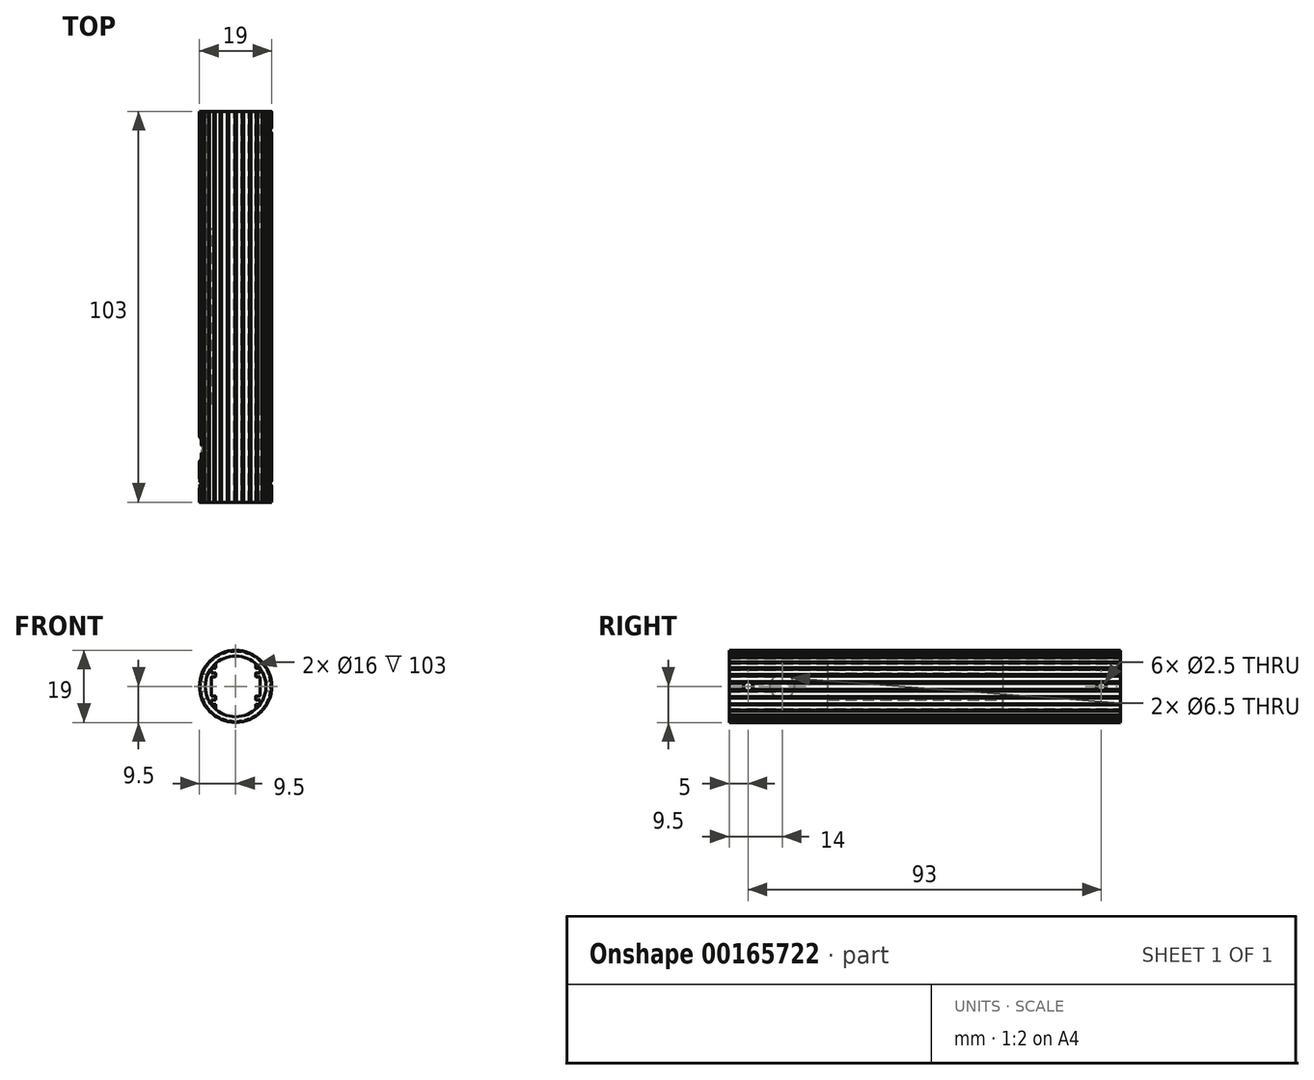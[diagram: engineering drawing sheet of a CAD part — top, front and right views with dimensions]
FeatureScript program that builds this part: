
annotation { "Feature Type Name" : "Feature", "Feature Type Description" : "" }
export const myFeature = defineFeature(function(context is Context, id is Id, definition is map)
    precondition{}
    {
        {
            assignVariable(context, id + "F0", {"name" : "Main_Length", "anyValue" : 103});
        }
        {
            assignVariable(context, id + "F1", {"name" : "Bore_Depth_F", "anyValue" : 26});
        }
        {
            assignVariable(context, id + "F2", {"name" : "Bore_Depth_R", "anyValue" : 31});
        }
        {
            var Q0;
            Q0=qCreatedBy(makeId("Front.planeOp"),FACE);
            var sketch = newSketch(context, id + "F3", { "sketchPlane" : qUnion([Q0])});
            skLineSegment(sketch, "E0", {"start": v(-5.25, -3.45) * mm, "end": v(-5.25, -2.65) * mm});
            skLineSegment(sketch, "E1", {"start": v(9.2, 1.38) * mm, "end": v(9.42, 1.2) * mm});
            skArc(sketch, "E2", {"start": v(-5.35, -2.55) * mm, "mid": v(-5.28, -2.58) * mm, "end": v(-5.25, -2.65) * mm});
            skArc(sketch, "E3", {"start": v(6.3, 4.75) * mm, "mid": v(6.37, 4.72) * mm, "end": v(6.4, 4.65) * mm});
            skArc(sketch, "E4", {"start": v(-5.25, -6.04) * mm, "mid": v(0, -8) * mm, "end": v(5.25, -6.04) * mm});
            skLineSegment(sketch, "E5", {"start": v(1.53, 9.17) * mm, "end": v(1.78, 9.33) * mm});
            skLineSegment(sketch, "E6", {"start": v(-7.18, -5.91) * mm, "end": v(-7.2, -6.2) * mm});
            skArc(sketch, "E7", {"start": v(-8.33, -4.58) * mm, "mid": v(-8.23, -4.75) * mm, "end": v(-8.13, -4.92) * mm});
            skLineSegment(sketch, "E8", {"start": v(5.13, 7.76) * mm, "end": v(5.42, 7.8) * mm});
            skLineSegment(sketch, "E9", {"start": v(6.4, -2.45) * mm, "end": v(6.4, 0) * mm});
            skLineSegment(sketch, "E10", {"start": v(-2.33, -9) * mm, "end": v(-2.17, -9.25) * mm});
            skArc(sketch, "E11", {"start": v(8.97, -3.13) * mm, "mid": v(9.04, -2.94) * mm, "end": v(9.1, -2.74) * mm});
            skArc(sketch, "E12", {"start": v(-4.05, -8.6) * mm, "mid": v(-3.86, -8.68) * mm, "end": v(-3.68, -8.76) * mm});
            skArc(sketch, "E13", {"start": v(4.05, 8.6) * mm, "mid": v(3.86, 8.68) * mm, "end": v(3.68, 8.76) * mm});
            skLineSegment(sketch, "E14", {"start": v(6.63, 6.52) * mm, "end": v(6.92, 6.5) * mm});
            skArc(sketch, "E15", {"start": v(-6.4, 3.65) * mm, "mid": v(-6.37, 3.58) * mm, "end": v(-6.3, 3.55) * mm});
            skArc(sketch, "E16", {"start": v(5.74, 7.57) * mm, "mid": v(5.58, 7.69) * mm, "end": v(5.42, 7.8) * mm});
            skLineSegment(sketch, "E17", {"start": v(-9.2, 1.38) * mm, "end": v(-9.42, 1.2) * mm});
            skArc(sketch, "E18", {"start": v(1.78, -9.33) * mm, "mid": v(1.98, -9.3) * mm, "end": v(2.17, -9.25) * mm});
            skLineSegment(sketch, "E19", {"start": v(-5.8, 7.28) * mm, "end": v(-5.74, 7.57) * mm});
            skArc(sketch, "E20", {"start": v(-2.17, -9.25) * mm, "mid": v(-1.98, -9.3) * mm, "end": v(-1.78, -9.33) * mm});
            skLineSegment(sketch, "E21", {"start": v(7.84, 5) * mm, "end": v(8.13, 4.92) * mm});
            skLineSegment(sketch, "E22", {"start": v(2.33, 9) * mm, "end": v(2.17, 9.25) * mm});
            skArc(sketch, "E23", {"start": v(5.25, -3.45) * mm, "mid": v(5.28, -3.52) * mm, "end": v(5.35, -3.55) * mm});
            skLineSegment(sketch, "E24", {"start": v(5.8, -7.28) * mm, "end": v(5.74, -7.57) * mm});
            skArc(sketch, "E25", {"start": v(5.35, 2.55) * mm, "mid": v(5.28, 2.58) * mm, "end": v(5.25, 2.65) * mm});
            skArc(sketch, "E26", {"start": v(4.15, -8.32) * mm, "mid": v(4.65, -8.05) * mm, "end": v(5.13, -7.76) * mm});
            skArc(sketch, "E27", {"start": v(-5.35, 4.75) * mm, "mid": v(-5.28, 4.78) * mm, "end": v(-5.25, 4.85) * mm});
            skArc(sketch, "E28", {"start": v(-8.13, 4.92) * mm, "mid": v(-8.23, 4.75) * mm, "end": v(-8.33, 4.58) * mm});
            skLineSegment(sketch, "E29", {"start": v(7.84, -5) * mm, "end": v(8.13, -4.92) * mm});
            skArc(sketch, "E30", {"start": v(8.33, 4.58) * mm, "mid": v(8.23, 4.75) * mm, "end": v(8.13, 4.92) * mm});
            skLineSegment(sketch, "E31", {"start": v(-6.3, 3.55) * mm, "end": v(-5.35, 3.55) * mm});
            skLineSegment(sketch, "E32", {"start": v(-5.25, 3.45) * mm, "end": v(-5.25, 2.65) * mm});
            skArc(sketch, "E33", {"start": v(9.1, 2.74) * mm, "mid": v(9.04, 2.94) * mm, "end": v(8.97, 3.13) * mm});
            skLineSegment(sketch, "E34", {"start": v(6.3, 3.55) * mm, "end": v(5.35, 3.55) * mm});
            skLineSegment(sketch, "E35", {"start": v(4.15, -8.32) * mm, "end": v(4.05, -8.6) * mm});
            skLineSegment(sketch, "E36", {"start": v(5.25, 6.04) * mm, "end": v(5.25, 4.85) * mm});
            skArc(sketch, "E37", {"start": v(8.71, 3.26) * mm, "mid": v(8.5, 3.78) * mm, "end": v(8.25, 4.3) * mm});
            skArc(sketch, "E38", {"start": v(0.4, -9.3) * mm, "mid": v(0.97, -9.25) * mm, "end": v(1.53, -9.17) * mm});
            skArc(sketch, "E39", {"start": v(9.47, 0.8) * mm, "mid": v(9.45, 1) * mm, "end": v(9.42, 1.2) * mm});
            skArc(sketch, "E40", {"start": v(-4.15, 8.32) * mm, "mid": v(-4.65, 8.05) * mm, "end": v(-5.13, 7.76) * mm});
            skLineSegment(sketch, "E41", {"start": v(-0.4, 9.3) * mm, "end": v(-0.2, 9.5) * mm});
            skLineSegment(sketch, "E42", {"start": v(8.25, 4.3) * mm, "end": v(8.33, 4.58) * mm});
            skLineSegment(sketch, "E43", {"start": v(2.33, -9) * mm, "end": v(2.17, -9.25) * mm});
            skArc(sketch, "E44", {"start": v(-0.4, 9.3) * mm, "mid": v(-0.97, 9.25) * mm, "end": v(-1.53, 9.17) * mm});
            skLineSegment(sketch, "E45", {"start": v(-5.13, 7.76) * mm, "end": v(-5.42, 7.8) * mm});
            skLineSegment(sketch, "E46", {"start": v(-2.33, 9) * mm, "end": v(-2.17, 9.25) * mm});
            skLineSegment(sketch, "E47", {"start": v(6.63, -6.52) * mm, "end": v(6.92, -6.5) * mm});
            skArc(sketch, "E48", {"start": v(9.42, -1.2) * mm, "mid": v(9.45, -1) * mm, "end": v(9.47, -0.8) * mm});
            skArc(sketch, "E49", {"start": v(-3.68, 8.76) * mm, "mid": v(-3.86, 8.68) * mm, "end": v(-4.05, 8.6) * mm});
            skArc(sketch, "E50", {"start": v(9.2, 1.38) * mm, "mid": v(9.1, 1.93) * mm, "end": v(8.96, 2.48) * mm});
            skArc(sketch, "E51", {"start": v(5.35, 4.75) * mm, "mid": v(5.28, 4.78) * mm, "end": v(5.25, 4.85) * mm});
            skLineSegment(sketch, "E52", {"start": v(5.25, 3.45) * mm, "end": v(5.25, 2.65) * mm});
            skArc(sketch, "E53", {"start": v(-0.2, -9.5) * mm, "mid": v(0, -9.5) * mm, "end": v(0.2, -9.5) * mm});
            skArc(sketch, "E54", {"start": v(7.2, 6.2) * mm, "mid": v(7.06, 6.36) * mm, "end": v(6.92, 6.5) * mm});
            skLineSegment(sketch, "E55", {"start": v(3.4, 8.65) * mm, "end": v(3.68, 8.76) * mm});
            skArc(sketch, "E56", {"start": v(6.4, 3.65) * mm, "mid": v(6.37, 3.58) * mm, "end": v(6.3, 3.55) * mm});
            skLineSegment(sketch, "E57", {"start": v(-6.4, -2.45) * mm, "end": v(-6.4, 0) * mm});
            skArc(sketch, "E58", {"start": v(-2.33, 9) * mm, "mid": v(-2.87, 8.84) * mm, "end": v(-3.4, 8.65) * mm});
            skLineSegment(sketch, "E59", {"start": v(-1.53, 9.17) * mm, "end": v(-1.78, 9.33) * mm});
            skLineSegment(sketch, "E60", {"start": v(0.4, -9.3) * mm, "end": v(0.2, -9.5) * mm});
            skArc(sketch, "E61", {"start": v(-6.92, 6.5) * mm, "mid": v(-7.06, 6.36) * mm, "end": v(-7.2, 6.2) * mm});
            skArc(sketch, "E62", {"start": v(-8.25, 4.3) * mm, "mid": v(-8.5, 3.78) * mm, "end": v(-8.71, 3.26) * mm});
            skArc(sketch, "E63", {"start": v(6.3, -4.75) * mm, "mid": v(6.37, -4.72) * mm, "end": v(6.4, -4.65) * mm});
            skLineSegment(sketch, "E64", {"start": v(-6.4, 4.65) * mm, "end": v(-6.4, 3.65) * mm});
            skLineSegment(sketch, "E65", {"start": v(-6.4, 2.45) * mm, "end": v(-6.4, 0) * mm});
            skArc(sketch, "E66", {"start": v(8.25, -4.3) * mm, "mid": v(8.5, -3.78) * mm, "end": v(8.71, -3.26) * mm});
            skArc(sketch, "E67", {"start": v(-6.3, 2.55) * mm, "mid": v(-6.37, 2.52) * mm, "end": v(-6.4, 2.45) * mm});
            skLineSegment(sketch, "E68", {"start": v(-5.25, 6.04) * mm, "end": v(-5.25, 4.85) * mm});
            skLineSegment(sketch, "E69", {"start": v(-5.35, 4.75) * mm, "end": v(-6.3, 4.75) * mm});
            skLineSegment(sketch, "E70", {"start": v(-5.35, 2.55) * mm, "end": v(-6.3, 2.55) * mm});
            skArc(sketch, "E71", {"start": v(-5.25, 3.45) * mm, "mid": v(-5.28, 3.52) * mm, "end": v(-5.35, 3.55) * mm});
            skArc(sketch, "E72", {"start": v(-5.35, 2.55) * mm, "mid": v(-5.28, 2.58) * mm, "end": v(-5.25, 2.65) * mm});
            skArc(sketch, "E73", {"start": v(-6.3, 4.75) * mm, "mid": v(-6.37, 4.72) * mm, "end": v(-6.4, 4.65) * mm});
            skArc(sketch, "E74", {"start": v(6.3, 2.55) * mm, "mid": v(6.37, 2.52) * mm, "end": v(6.4, 2.45) * mm});
            skLineSegment(sketch, "E75", {"start": v(5.35, 2.55) * mm, "end": v(6.3, 2.55) * mm});
            skArc(sketch, "E76", {"start": v(5.25, 3.45) * mm, "mid": v(5.28, 3.52) * mm, "end": v(5.35, 3.55) * mm});
            skArc(sketch, "E77", {"start": v(0.2, 9.5) * mm, "mid": v(0, 9.5) * mm, "end": v(-0.2, 9.5) * mm});
            skLineSegment(sketch, "E78", {"start": v(5.35, 4.75) * mm, "end": v(6.3, 4.75) * mm});
            skLineSegment(sketch, "E79", {"start": v(6.4, 2.45) * mm, "end": v(6.4, 0) * mm});
            skLineSegment(sketch, "E80", {"start": v(6.4, 4.65) * mm, "end": v(6.4, 3.65) * mm});
            skArc(sketch, "E81", {"start": v(-5.35, -4.75) * mm, "mid": v(-5.28, -4.78) * mm, "end": v(-5.25, -4.85) * mm});
            skLineSegment(sketch, "E82", {"start": v(-6.3, -3.55) * mm, "end": v(-5.35, -3.55) * mm});
            skLineSegment(sketch, "E83", {"start": v(-5.35, -2.55) * mm, "end": v(-6.3, -2.55) * mm});
            skArc(sketch, "E84", {"start": v(-5.25, -3.45) * mm, "mid": v(-5.28, -3.52) * mm, "end": v(-5.35, -3.55) * mm});
            skArc(sketch, "E85", {"start": v(-6.3, -2.55) * mm, "mid": v(-6.37, -2.52) * mm, "end": v(-6.4, -2.45) * mm});
            skArc(sketch, "E86", {"start": v(-6.4, -3.65) * mm, "mid": v(-6.37, -3.58) * mm, "end": v(-6.3, -3.55) * mm});
            skArc(sketch, "E87", {"start": v(-6.3, -4.75) * mm, "mid": v(-6.37, -4.72) * mm, "end": v(-6.4, -4.65) * mm});
            skArc(sketch, "E88", {"start": v(5.35, -2.55) * mm, "mid": v(5.28, -2.58) * mm, "end": v(5.25, -2.65) * mm});
            skLineSegment(sketch, "E89", {"start": v(-3.4, 8.65) * mm, "end": v(-3.68, 8.76) * mm});
            skArc(sketch, "E90", {"start": v(6.3, -2.55) * mm, "mid": v(6.37, -2.52) * mm, "end": v(6.4, -2.45) * mm});
            skLineSegment(sketch, "E91", {"start": v(5.35, -2.55) * mm, "end": v(6.3, -2.55) * mm});
            skArc(sketch, "E92", {"start": v(6.4, -3.65) * mm, "mid": v(6.37, -3.58) * mm, "end": v(6.3, -3.55) * mm});
            skLineSegment(sketch, "E93", {"start": v(6.3, -3.55) * mm, "end": v(5.35, -3.55) * mm});
            skArc(sketch, "E94", {"start": v(5.35, -4.75) * mm, "mid": v(5.28, -4.78) * mm, "end": v(5.25, -4.85) * mm});
            skLineSegment(sketch, "E95", {"start": v(-5.25, -6.04) * mm, "end": v(-5.25, -4.85) * mm});
            skLineSegment(sketch, "E96", {"start": v(5.25, -3.45) * mm, "end": v(5.25, -2.65) * mm});
            skLineSegment(sketch, "E97", {"start": v(6.4, -4.65) * mm, "end": v(6.4, -3.65) * mm});
            skLineSegment(sketch, "E98", {"start": v(-5.35, -4.75) * mm, "end": v(-6.3, -4.75) * mm});
            skArc(sketch, "E99", {"start": v(-8.97, 3.13) * mm, "mid": v(-9.04, 2.94) * mm, "end": v(-9.1, 2.74) * mm});
            skLineSegment(sketch, "E100", {"start": v(-6.4, -4.65) * mm, "end": v(-6.4, -3.65) * mm});
            skLineSegment(sketch, "E101", {"start": v(5.35, -4.75) * mm, "end": v(6.3, -4.75) * mm});
            skLineSegment(sketch, "E102", {"start": v(-7.84, 5) * mm, "end": v(-8.13, 4.92) * mm});
            skLineSegment(sketch, "E103", {"start": v(5.25, -6.04) * mm, "end": v(5.25, -4.85) * mm});
            skArc(sketch, "E104", {"start": v(5.25, 6.04) * mm, "mid": v(0, 8) * mm, "end": v(-5.25, 6.04) * mm});
            skLineSegment(sketch, "E105", {"start": v(-0.4, -9.3) * mm, "end": v(-0.2, -9.5) * mm});
            skArc(sketch, "E106", {"start": v(2.33, -9) * mm, "mid": v(2.87, -8.84) * mm, "end": v(3.4, -8.65) * mm});
            skLineSegment(sketch, "E107", {"start": v(1.53, -9.17) * mm, "end": v(1.78, -9.33) * mm});
            skArc(sketch, "E108", {"start": v(3.68, -8.76) * mm, "mid": v(3.86, -8.68) * mm, "end": v(4.05, -8.6) * mm});
            skArc(sketch, "E109", {"start": v(-9.1, -2.74) * mm, "mid": v(-9.04, -2.94) * mm, "end": v(-8.97, -3.13) * mm});
            skLineSegment(sketch, "E110", {"start": v(3.4, -8.65) * mm, "end": v(3.68, -8.76) * mm});
            skArc(sketch, "E111", {"start": v(5.8, -7.28) * mm, "mid": v(6.22, -6.91) * mm, "end": v(6.63, -6.52) * mm});
            skArc(sketch, "E112", {"start": v(5.42, -7.8) * mm, "mid": v(5.58, -7.69) * mm, "end": v(5.74, -7.57) * mm});
            skLineSegment(sketch, "E113", {"start": v(5.13, -7.76) * mm, "end": v(5.42, -7.8) * mm});
            skLineSegment(sketch, "E114", {"start": v(-5.13, -7.76) * mm, "end": v(-5.42, -7.8) * mm});
            skLineSegment(sketch, "E115", {"start": v(7.18, -5.91) * mm, "end": v(7.2, -6.2) * mm});
            skLineSegment(sketch, "E116", {"start": v(-6.63, -6.52) * mm, "end": v(-6.92, -6.5) * mm});
            skArc(sketch, "E117", {"start": v(8.13, -4.92) * mm, "mid": v(8.23, -4.75) * mm, "end": v(8.33, -4.58) * mm});
            skArc(sketch, "E118", {"start": v(6.92, -6.5) * mm, "mid": v(7.06, -6.36) * mm, "end": v(7.2, -6.2) * mm});
            skArc(sketch, "E119", {"start": v(-5.74, -7.57) * mm, "mid": v(-5.58, -7.69) * mm, "end": v(-5.42, -7.8) * mm});
            skArc(sketch, "E120", {"start": v(8.96, -2.48) * mm, "mid": v(9.1, -1.93) * mm, "end": v(9.2, -1.38) * mm});
            skLineSegment(sketch, "E121", {"start": v(8.96, -2.48) * mm, "end": v(9.1, -2.74) * mm});
            skLineSegment(sketch, "E122", {"start": v(8.71, -3.26) * mm, "end": v(8.97, -3.13) * mm});
            skArc(sketch, "E123", {"start": v(9.28, -0.57) * mm, "mid": v(9.3, 0) * mm, "end": v(9.28, 0.57) * mm});
            skLineSegment(sketch, "E124", {"start": v(9.28, -0.57) * mm, "end": v(9.47, -0.8) * mm});
            skLineSegment(sketch, "E125", {"start": v(-1.53, -9.17) * mm, "end": v(-1.78, -9.33) * mm});
            skLineSegment(sketch, "E126", {"start": v(9.2, -1.38) * mm, "end": v(9.42, -1.2) * mm});
            skLineSegment(sketch, "E127", {"start": v(8.71, 3.26) * mm, "end": v(8.97, 3.13) * mm});
            skLineSegment(sketch, "E128", {"start": v(8.96, 2.48) * mm, "end": v(9.1, 2.74) * mm});
            skArc(sketch, "E129", {"start": v(7.84, 5) * mm, "mid": v(7.52, 5.47) * mm, "end": v(7.18, 5.91) * mm});
            skArc(sketch, "E130", {"start": v(6.63, 6.52) * mm, "mid": v(6.22, 6.91) * mm, "end": v(5.8, 7.28) * mm});
            skLineSegment(sketch, "E131", {"start": v(7.18, 5.91) * mm, "end": v(7.2, 6.2) * mm});
            skArc(sketch, "E132", {"start": v(5.13, 7.76) * mm, "mid": v(4.65, 8.05) * mm, "end": v(4.15, 8.32) * mm});
            skLineSegment(sketch, "E133", {"start": v(5.8, 7.28) * mm, "end": v(5.74, 7.57) * mm});
            skArc(sketch, "E134", {"start": v(3.4, 8.65) * mm, "mid": v(2.87, 8.84) * mm, "end": v(2.33, 9) * mm});
            skLineSegment(sketch, "E135", {"start": v(4.15, 8.32) * mm, "end": v(4.05, 8.6) * mm});
            skArc(sketch, "E136", {"start": v(1.53, 9.17) * mm, "mid": v(0.97, 9.25) * mm, "end": v(0.4, 9.3) * mm});
            skArc(sketch, "E137", {"start": v(2.17, 9.25) * mm, "mid": v(1.98, 9.3) * mm, "end": v(1.78, 9.33) * mm});
            skLineSegment(sketch, "E138", {"start": v(0.4, 9.3) * mm, "end": v(0.2, 9.5) * mm});
            skArc(sketch, "E139", {"start": v(-1.78, 9.33) * mm, "mid": v(-1.98, 9.3) * mm, "end": v(-2.17, 9.25) * mm});
            skLineSegment(sketch, "E140", {"start": v(-4.15, 8.32) * mm, "end": v(-4.05, 8.6) * mm});
            skArc(sketch, "E141", {"start": v(-5.8, 7.28) * mm, "mid": v(-6.22, 6.91) * mm, "end": v(-6.63, 6.52) * mm});
            skArc(sketch, "E142", {"start": v(-5.42, 7.8) * mm, "mid": v(-5.58, 7.69) * mm, "end": v(-5.74, 7.57) * mm});
            skLineSegment(sketch, "E143", {"start": v(-9.2, -1.38) * mm, "end": v(-9.42, -1.2) * mm});
            skLineSegment(sketch, "E144", {"start": v(-7.18, 5.91) * mm, "end": v(-7.2, 6.2) * mm});
            skLineSegment(sketch, "E145", {"start": v(-6.63, 6.52) * mm, "end": v(-6.92, 6.5) * mm});
            skArc(sketch, "E146", {"start": v(-8.96, 2.48) * mm, "mid": v(-9.1, 1.93) * mm, "end": v(-9.2, 1.38) * mm});
            skLineSegment(sketch, "E147", {"start": v(-8.96, 2.48) * mm, "end": v(-9.1, 2.74) * mm});
            skLineSegment(sketch, "E148", {"start": v(-8.71, 3.26) * mm, "end": v(-8.97, 3.13) * mm});
            skArc(sketch, "E149", {"start": v(-9.28, 0.57) * mm, "mid": v(-9.3, 0) * mm, "end": v(-9.28, -0.57) * mm});
            skArc(sketch, "E150", {"start": v(-9.42, 1.2) * mm, "mid": v(-9.45, 1) * mm, "end": v(-9.47, 0.8) * mm});
            skLineSegment(sketch, "E151", {"start": v(-9.28, 0.57) * mm, "end": v(-9.47, 0.8) * mm});
            skLineSegment(sketch, "E152", {"start": v(8.25, -4.3) * mm, "end": v(8.33, -4.58) * mm});
            skArc(sketch, "E153", {"start": v(-9.2, -1.38) * mm, "mid": v(-9.1, -1.93) * mm, "end": v(-8.96, -2.48) * mm});
            skArc(sketch, "E154", {"start": v(-9.47, -0.8) * mm, "mid": v(-9.45, -1) * mm, "end": v(-9.42, -1.2) * mm});
            skLineSegment(sketch, "E155", {"start": v(-9.28, -0.57) * mm, "end": v(-9.47, -0.8) * mm});
            skArc(sketch, "E156", {"start": v(-8.71, -3.26) * mm, "mid": v(-8.5, -3.78) * mm, "end": v(-8.25, -4.3) * mm});
            skLineSegment(sketch, "E157", {"start": v(-8.71, -3.26) * mm, "end": v(-8.97, -3.13) * mm});
            skLineSegment(sketch, "E158", {"start": v(-8.96, -2.48) * mm, "end": v(-9.1, -2.74) * mm});
            skArc(sketch, "E159", {"start": v(-7.84, -5) * mm, "mid": v(-7.52, -5.47) * mm, "end": v(-7.18, -5.91) * mm});
            skLineSegment(sketch, "E160", {"start": v(-7.84, -5) * mm, "end": v(-8.13, -4.92) * mm});
            skLineSegment(sketch, "E161", {"start": v(-8.25, -4.3) * mm, "end": v(-8.33, -4.58) * mm});
            skArc(sketch, "E162", {"start": v(-6.63, -6.52) * mm, "mid": v(-6.22, -6.91) * mm, "end": v(-5.8, -7.28) * mm});
            skLineSegment(sketch, "E163", {"start": v(9.28, 0.57) * mm, "end": v(9.47, 0.8) * mm});
            skArc(sketch, "E164", {"start": v(-7.2, -6.2) * mm, "mid": v(-7.06, -6.36) * mm, "end": v(-6.92, -6.5) * mm});
            skArc(sketch, "E165", {"start": v(7.18, -5.91) * mm, "mid": v(7.52, -5.47) * mm, "end": v(7.84, -5) * mm});
            skLineSegment(sketch, "E166", {"start": v(-5.8, -7.28) * mm, "end": v(-5.74, -7.57) * mm});
            skArc(sketch, "E167", {"start": v(-3.4, -8.65) * mm, "mid": v(-2.87, -8.84) * mm, "end": v(-2.33, -9) * mm});
            skLineSegment(sketch, "E168", {"start": v(-3.4, -8.65) * mm, "end": v(-3.68, -8.76) * mm});
            skLineSegment(sketch, "E169", {"start": v(-4.15, -8.32) * mm, "end": v(-4.05, -8.6) * mm});
            skArc(sketch, "E170", {"start": v(-1.53, -9.17) * mm, "mid": v(-0.97, -9.25) * mm, "end": v(-0.4, -9.3) * mm});
            skArc(sketch, "E171", {"start": v(-7.18, 5.91) * mm, "mid": v(-7.52, 5.47) * mm, "end": v(-7.84, 5) * mm});
            skLineSegment(sketch, "E172", {"start": v(-8.25, 4.3) * mm, "end": v(-8.33, 4.58) * mm});
            skArc(sketch, "E173", {"start": v(-5.13, -7.76) * mm, "mid": v(-4.65, -8.05) * mm, "end": v(-4.15, -8.32) * mm});
            skSolve(sketch);
        }
        {
            var Q0;
            Q0=makeQuery(id+"F3.imprint","IMPRINT",FACE,{"disambiguationData":[TD([[makeQuery(id+"F3.imprint","IMPRINT",EDGE,{"derivedFrom":sQuery(id+"F3.wireOp",EDGE,"E0")}),1.0]])]});
            extrude(context, id + "F4", {"entities" : qUnion([Q0]), "depth" : (getVariable(context, 'Main_Length') - getVariable(context, 'Bore_Depth_F') - getVariable(context, 'Bore_Depth_R')) * mm});
        }
        {
            var Q0;
            Q0=makeQuery(id+"F4.opExtrude","CAP_FACE",FACE,{"disambiguationData":[OSD([sQuery(id+"F3.wireOp",EDGE,"E0"),sQuery(id+"F3.wireOp",EDGE,"E1"),sQuery(id+"F3.wireOp",EDGE,"E2"),sQuery(id+"F3.wireOp",EDGE,"E3"),sQuery(id+"F3.wireOp",EDGE,"E4"),sQuery(id+"F3.wireOp",EDGE,"E5"),sQuery(id+"F3.wireOp",EDGE,"E6"),sQuery(id+"F3.wireOp",EDGE,"E7"),sQuery(id+"F3.wireOp",EDGE,"E8"),sQuery(id+"F3.wireOp",EDGE,"E9"),sQuery(id+"F3.wireOp",EDGE,"E10"),sQuery(id+"F3.wireOp",EDGE,"E11"),sQuery(id+"F3.wireOp",EDGE,"E12"),sQuery(id+"F3.wireOp",EDGE,"E13"),sQuery(id+"F3.wireOp",EDGE,"E14"),sQuery(id+"F3.wireOp",EDGE,"E15"),sQuery(id+"F3.wireOp",EDGE,"E16"),sQuery(id+"F3.wireOp",EDGE,"E17"),sQuery(id+"F3.wireOp",EDGE,"E18"),sQuery(id+"F3.wireOp",EDGE,"E19"),sQuery(id+"F3.wireOp",EDGE,"E20"),sQuery(id+"F3.wireOp",EDGE,"E21"),sQuery(id+"F3.wireOp",EDGE,"E22"),sQuery(id+"F3.wireOp",EDGE,"E23"),sQuery(id+"F3.wireOp",EDGE,"E24"),sQuery(id+"F3.wireOp",EDGE,"E25"),sQuery(id+"F3.wireOp",EDGE,"E26"),sQuery(id+"F3.wireOp",EDGE,"E27"),sQuery(id+"F3.wireOp",EDGE,"E28"),sQuery(id+"F3.wireOp",EDGE,"E29"),sQuery(id+"F3.wireOp",EDGE,"E30"),sQuery(id+"F3.wireOp",EDGE,"E31"),sQuery(id+"F3.wireOp",EDGE,"E32"),sQuery(id+"F3.wireOp",EDGE,"E33"),sQuery(id+"F3.wireOp",EDGE,"E34"),sQuery(id+"F3.wireOp",EDGE,"E35"),sQuery(id+"F3.wireOp",EDGE,"E36"),sQuery(id+"F3.wireOp",EDGE,"E37"),sQuery(id+"F3.wireOp",EDGE,"E38"),sQuery(id+"F3.wireOp",EDGE,"E39"),sQuery(id+"F3.wireOp",EDGE,"E40"),sQuery(id+"F3.wireOp",EDGE,"E41"),sQuery(id+"F3.wireOp",EDGE,"E42"),sQuery(id+"F3.wireOp",EDGE,"E43"),sQuery(id+"F3.wireOp",EDGE,"E44"),sQuery(id+"F3.wireOp",EDGE,"E45"),sQuery(id+"F3.wireOp",EDGE,"E46"),sQuery(id+"F3.wireOp",EDGE,"E47"),sQuery(id+"F3.wireOp",EDGE,"E48"),sQuery(id+"F3.wireOp",EDGE,"E49"),sQuery(id+"F3.wireOp",EDGE,"E50"),sQuery(id+"F3.wireOp",EDGE,"E51"),sQuery(id+"F3.wireOp",EDGE,"E52"),sQuery(id+"F3.wireOp",EDGE,"E53"),sQuery(id+"F3.wireOp",EDGE,"E54"),sQuery(id+"F3.wireOp",EDGE,"E55"),sQuery(id+"F3.wireOp",EDGE,"E56"),sQuery(id+"F3.wireOp",EDGE,"E57"),sQuery(id+"F3.wireOp",EDGE,"E58"),sQuery(id+"F3.wireOp",EDGE,"E59"),sQuery(id+"F3.wireOp",EDGE,"E60"),sQuery(id+"F3.wireOp",EDGE,"E61"),sQuery(id+"F3.wireOp",EDGE,"E62"),sQuery(id+"F3.wireOp",EDGE,"E63"),sQuery(id+"F3.wireOp",EDGE,"E64"),sQuery(id+"F3.wireOp",EDGE,"E65"),sQuery(id+"F3.wireOp",EDGE,"E66"),sQuery(id+"F3.wireOp",EDGE,"E67"),sQuery(id+"F3.wireOp",EDGE,"E68"),sQuery(id+"F3.wireOp",EDGE,"E69"),sQuery(id+"F3.wireOp",EDGE,"E70"),sQuery(id+"F3.wireOp",EDGE,"E71"),sQuery(id+"F3.wireOp",EDGE,"E72"),sQuery(id+"F3.wireOp",EDGE,"E73"),sQuery(id+"F3.wireOp",EDGE,"E74"),sQuery(id+"F3.wireOp",EDGE,"E75"),sQuery(id+"F3.wireOp",EDGE,"E76"),sQuery(id+"F3.wireOp",EDGE,"E77"),sQuery(id+"F3.wireOp",EDGE,"E78"),sQuery(id+"F3.wireOp",EDGE,"E79"),sQuery(id+"F3.wireOp",EDGE,"E80"),sQuery(id+"F3.wireOp",EDGE,"E81"),sQuery(id+"F3.wireOp",EDGE,"E82"),sQuery(id+"F3.wireOp",EDGE,"E83"),sQuery(id+"F3.wireOp",EDGE,"E84"),sQuery(id+"F3.wireOp",EDGE,"E85"),sQuery(id+"F3.wireOp",EDGE,"E86"),sQuery(id+"F3.wireOp",EDGE,"E87"),sQuery(id+"F3.wireOp",EDGE,"E88"),sQuery(id+"F3.wireOp",EDGE,"E89"),sQuery(id+"F3.wireOp",EDGE,"E90"),sQuery(id+"F3.wireOp",EDGE,"E91"),sQuery(id+"F3.wireOp",EDGE,"E92"),sQuery(id+"F3.wireOp",EDGE,"E93"),sQuery(id+"F3.wireOp",EDGE,"E94"),sQuery(id+"F3.wireOp",EDGE,"E95"),sQuery(id+"F3.wireOp",EDGE,"E96"),sQuery(id+"F3.wireOp",EDGE,"E97"),sQuery(id+"F3.wireOp",EDGE,"E98"),sQuery(id+"F3.wireOp",EDGE,"E99"),sQuery(id+"F3.wireOp",EDGE,"E100"),sQuery(id+"F3.wireOp",EDGE,"E101"),sQuery(id+"F3.wireOp",EDGE,"E102"),sQuery(id+"F3.wireOp",EDGE,"E103"),sQuery(id+"F3.wireOp",EDGE,"E104"),sQuery(id+"F3.wireOp",EDGE,"E105"),sQuery(id+"F3.wireOp",EDGE,"E106"),sQuery(id+"F3.wireOp",EDGE,"E107"),sQuery(id+"F3.wireOp",EDGE,"E108"),sQuery(id+"F3.wireOp",EDGE,"E109"),sQuery(id+"F3.wireOp",EDGE,"E110"),sQuery(id+"F3.wireOp",EDGE,"E111"),sQuery(id+"F3.wireOp",EDGE,"E112"),sQuery(id+"F3.wireOp",EDGE,"E113"),sQuery(id+"F3.wireOp",EDGE,"E114"),sQuery(id+"F3.wireOp",EDGE,"E115"),sQuery(id+"F3.wireOp",EDGE,"E116"),sQuery(id+"F3.wireOp",EDGE,"E117"),sQuery(id+"F3.wireOp",EDGE,"E118"),sQuery(id+"F3.wireOp",EDGE,"E119"),sQuery(id+"F3.wireOp",EDGE,"E120"),sQuery(id+"F3.wireOp",EDGE,"E121"),sQuery(id+"F3.wireOp",EDGE,"E122"),sQuery(id+"F3.wireOp",EDGE,"E123"),sQuery(id+"F3.wireOp",EDGE,"E124"),sQuery(id+"F3.wireOp",EDGE,"E125"),sQuery(id+"F3.wireOp",EDGE,"E126"),sQuery(id+"F3.wireOp",EDGE,"E127"),sQuery(id+"F3.wireOp",EDGE,"E128"),sQuery(id+"F3.wireOp",EDGE,"E129"),sQuery(id+"F3.wireOp",EDGE,"E130"),sQuery(id+"F3.wireOp",EDGE,"E131"),sQuery(id+"F3.wireOp",EDGE,"E132"),sQuery(id+"F3.wireOp",EDGE,"E133"),sQuery(id+"F3.wireOp",EDGE,"E134"),sQuery(id+"F3.wireOp",EDGE,"E135"),sQuery(id+"F3.wireOp",EDGE,"E136"),sQuery(id+"F3.wireOp",EDGE,"E137"),sQuery(id+"F3.wireOp",EDGE,"E138"),sQuery(id+"F3.wireOp",EDGE,"E139"),sQuery(id+"F3.wireOp",EDGE,"E140"),sQuery(id+"F3.wireOp",EDGE,"E141"),sQuery(id+"F3.wireOp",EDGE,"E142"),sQuery(id+"F3.wireOp",EDGE,"E143"),sQuery(id+"F3.wireOp",EDGE,"E144"),sQuery(id+"F3.wireOp",EDGE,"E145"),sQuery(id+"F3.wireOp",EDGE,"E146"),sQuery(id+"F3.wireOp",EDGE,"E147"),sQuery(id+"F3.wireOp",EDGE,"E148"),sQuery(id+"F3.wireOp",EDGE,"E149"),sQuery(id+"F3.wireOp",EDGE,"E150"),sQuery(id+"F3.wireOp",EDGE,"E151"),sQuery(id+"F3.wireOp",EDGE,"E152"),sQuery(id+"F3.wireOp",EDGE,"E153"),sQuery(id+"F3.wireOp",EDGE,"E154"),sQuery(id+"F3.wireOp",EDGE,"E155"),sQuery(id+"F3.wireOp",EDGE,"E156"),sQuery(id+"F3.wireOp",EDGE,"E157"),sQuery(id+"F3.wireOp",EDGE,"E158"),sQuery(id+"F3.wireOp",EDGE,"E159"),sQuery(id+"F3.wireOp",EDGE,"E160"),sQuery(id+"F3.wireOp",EDGE,"E161"),sQuery(id+"F3.wireOp",EDGE,"E162"),sQuery(id+"F3.wireOp",EDGE,"E163"),sQuery(id+"F3.wireOp",EDGE,"E164"),sQuery(id+"F3.wireOp",EDGE,"E165"),sQuery(id+"F3.wireOp",EDGE,"E166"),sQuery(id+"F3.wireOp",EDGE,"E167"),sQuery(id+"F3.wireOp",EDGE,"E168"),sQuery(id+"F3.wireOp",EDGE,"E169"),sQuery(id+"F3.wireOp",EDGE,"E170"),sQuery(id+"F3.wireOp",EDGE,"E171"),sQuery(id+"F3.wireOp",EDGE,"E172"),sQuery(id+"F3.wireOp",EDGE,"E173")])],"isStart":false});
            var sketch = newSketch(context, id + "F5", { "sketchPlane" : qUnion([Q0])});
            skCircle(sketch, "E174", {"center": v(0, 0) * mm, "radius": 8 * mm});
            skLineSegment(sketch, "E175.0.0", {"start": v(9.42, 1.2) * mm, "end": v(9.2, 1.38) * mm});
            skArc(sketch, "E175.0.1", {"start": v(9.2, 1.38) * mm, "mid": v(9.1, 1.93) * mm, "end": v(8.96, 2.48) * mm});
            skLineSegment(sketch, "E175.0.2", {"start": v(8.96, 2.48) * mm, "end": v(9.1, 2.74) * mm});
            skArc(sketch, "E175.0.3", {"start": v(9.1, 2.74) * mm, "mid": v(9.04, 2.94) * mm, "end": v(8.97, 3.13) * mm});
            skLineSegment(sketch, "E175.0.4", {"start": v(8.97, 3.13) * mm, "end": v(8.71, 3.26) * mm});
            skArc(sketch, "E175.0.5", {"start": v(8.71, 3.26) * mm, "mid": v(8.5, 3.78) * mm, "end": v(8.25, 4.3) * mm});
            skLineSegment(sketch, "E175.0.6", {"start": v(8.25, 4.3) * mm, "end": v(8.33, 4.58) * mm});
            skArc(sketch, "E175.0.7", {"start": v(8.33, 4.58) * mm, "mid": v(8.23, 4.75) * mm, "end": v(8.13, 4.92) * mm});
            skLineSegment(sketch, "E175.0.8", {"start": v(8.13, 4.92) * mm, "end": v(7.84, 5) * mm});
            skArc(sketch, "E175.0.9", {"start": v(7.84, 5) * mm, "mid": v(7.52, 5.47) * mm, "end": v(7.18, 5.91) * mm});
            skLineSegment(sketch, "E175.0.10", {"start": v(7.18, 5.91) * mm, "end": v(7.2, 6.2) * mm});
            skArc(sketch, "E175.0.11", {"start": v(7.2, 6.2) * mm, "mid": v(7.06, 6.36) * mm, "end": v(6.92, 6.5) * mm});
            skLineSegment(sketch, "E175.0.12", {"start": v(6.92, 6.5) * mm, "end": v(6.63, 6.52) * mm});
            skArc(sketch, "E175.0.13", {"start": v(6.63, 6.52) * mm, "mid": v(6.22, 6.91) * mm, "end": v(5.8, 7.28) * mm});
            skLineSegment(sketch, "E175.0.14", {"start": v(5.8, 7.28) * mm, "end": v(5.74, 7.57) * mm});
            skArc(sketch, "E175.0.15", {"start": v(5.74, 7.57) * mm, "mid": v(5.58, 7.69) * mm, "end": v(5.42, 7.8) * mm});
            skLineSegment(sketch, "E175.0.16", {"start": v(5.42, 7.8) * mm, "end": v(5.13, 7.76) * mm});
            skArc(sketch, "E175.0.17", {"start": v(5.13, 7.76) * mm, "mid": v(4.65, 8.05) * mm, "end": v(4.15, 8.32) * mm});
            skLineSegment(sketch, "E175.0.18", {"start": v(4.15, 8.32) * mm, "end": v(4.05, 8.6) * mm});
            skArc(sketch, "E175.0.19", {"start": v(4.05, 8.6) * mm, "mid": v(3.86, 8.68) * mm, "end": v(3.68, 8.76) * mm});
            skLineSegment(sketch, "E175.0.20", {"start": v(3.68, 8.76) * mm, "end": v(3.4, 8.65) * mm});
            skArc(sketch, "E175.0.21", {"start": v(3.4, 8.65) * mm, "mid": v(2.87, 8.84) * mm, "end": v(2.33, 9) * mm});
            skLineSegment(sketch, "E175.0.22", {"start": v(2.33, 9) * mm, "end": v(2.17, 9.25) * mm});
            skArc(sketch, "E175.0.23", {"start": v(2.17, 9.25) * mm, "mid": v(1.98, 9.3) * mm, "end": v(1.78, 9.33) * mm});
            skLineSegment(sketch, "E175.0.24", {"start": v(1.78, 9.33) * mm, "end": v(1.53, 9.17) * mm});
            skArc(sketch, "E175.0.25", {"start": v(1.53, 9.17) * mm, "mid": v(0.97, 9.25) * mm, "end": v(0.4, 9.3) * mm});
            skLineSegment(sketch, "E175.0.26", {"start": v(0.4, 9.3) * mm, "end": v(0.2, 9.5) * mm});
            skArc(sketch, "E175.0.27", {"start": v(0.2, 9.5) * mm, "mid": v(0, 9.5) * mm, "end": v(-0.2, 9.5) * mm});
            skLineSegment(sketch, "E175.0.28", {"start": v(-0.2, 9.5) * mm, "end": v(-0.4, 9.3) * mm});
            skArc(sketch, "E175.0.29", {"start": v(-0.4, 9.3) * mm, "mid": v(-0.97, 9.25) * mm, "end": v(-1.53, 9.17) * mm});
            skLineSegment(sketch, "E175.0.30", {"start": v(-1.53, 9.17) * mm, "end": v(-1.78, 9.33) * mm});
            skArc(sketch, "E175.0.31", {"start": v(-1.78, 9.33) * mm, "mid": v(-1.98, 9.3) * mm, "end": v(-2.17, 9.25) * mm});
            skLineSegment(sketch, "E175.0.32", {"start": v(-2.17, 9.25) * mm, "end": v(-2.33, 9) * mm});
            skArc(sketch, "E175.0.33", {"start": v(-2.33, 9) * mm, "mid": v(-2.87, 8.84) * mm, "end": v(-3.4, 8.65) * mm});
            skLineSegment(sketch, "E175.0.34", {"start": v(-3.4, 8.65) * mm, "end": v(-3.68, 8.76) * mm});
            skArc(sketch, "E175.0.35", {"start": v(-3.68, 8.76) * mm, "mid": v(-3.86, 8.68) * mm, "end": v(-4.05, 8.6) * mm});
            skLineSegment(sketch, "E175.0.36", {"start": v(-4.05, 8.6) * mm, "end": v(-4.15, 8.32) * mm});
            skArc(sketch, "E175.0.37", {"start": v(-4.15, 8.32) * mm, "mid": v(-4.65, 8.05) * mm, "end": v(-5.13, 7.76) * mm});
            skLineSegment(sketch, "E175.0.38", {"start": v(-5.13, 7.76) * mm, "end": v(-5.42, 7.8) * mm});
            skArc(sketch, "E175.0.39", {"start": v(-5.42, 7.8) * mm, "mid": v(-5.58, 7.69) * mm, "end": v(-5.74, 7.57) * mm});
            skLineSegment(sketch, "E175.0.40", {"start": v(-5.74, 7.57) * mm, "end": v(-5.8, 7.28) * mm});
            skArc(sketch, "E175.0.41", {"start": v(-5.8, 7.28) * mm, "mid": v(-6.22, 6.91) * mm, "end": v(-6.63, 6.52) * mm});
            skLineSegment(sketch, "E175.0.42", {"start": v(-6.63, 6.52) * mm, "end": v(-6.92, 6.5) * mm});
            skArc(sketch, "E175.0.43", {"start": v(-6.92, 6.5) * mm, "mid": v(-7.06, 6.36) * mm, "end": v(-7.2, 6.2) * mm});
            skLineSegment(sketch, "E175.0.44", {"start": v(-7.2, 6.2) * mm, "end": v(-7.18, 5.91) * mm});
            skArc(sketch, "E175.0.45", {"start": v(-7.18, 5.91) * mm, "mid": v(-7.52, 5.47) * mm, "end": v(-7.84, 5) * mm});
            skLineSegment(sketch, "E175.0.46", {"start": v(-7.84, 5) * mm, "end": v(-8.13, 4.92) * mm});
            skArc(sketch, "E175.0.47", {"start": v(-8.13, 4.92) * mm, "mid": v(-8.23, 4.75) * mm, "end": v(-8.33, 4.58) * mm});
            skLineSegment(sketch, "E175.0.48", {"start": v(-8.33, 4.58) * mm, "end": v(-8.25, 4.3) * mm});
            skArc(sketch, "E175.0.49", {"start": v(-8.25, 4.3) * mm, "mid": v(-8.5, 3.78) * mm, "end": v(-8.71, 3.26) * mm});
            skLineSegment(sketch, "E175.0.50", {"start": v(-8.71, 3.26) * mm, "end": v(-8.97, 3.13) * mm});
            skArc(sketch, "E175.0.51", {"start": v(-8.97, 3.13) * mm, "mid": v(-9.04, 2.94) * mm, "end": v(-9.1, 2.74) * mm});
            skLineSegment(sketch, "E175.0.52", {"start": v(-9.1, 2.74) * mm, "end": v(-8.96, 2.48) * mm});
            skArc(sketch, "E175.0.53", {"start": v(-8.96, 2.48) * mm, "mid": v(-9.1, 1.93) * mm, "end": v(-9.2, 1.38) * mm});
            skLineSegment(sketch, "E175.0.54", {"start": v(-9.2, 1.38) * mm, "end": v(-9.42, 1.2) * mm});
            skArc(sketch, "E175.0.55", {"start": v(-9.42, 1.2) * mm, "mid": v(-9.45, 1) * mm, "end": v(-9.47, 0.8) * mm});
            skLineSegment(sketch, "E175.0.56", {"start": v(-9.47, 0.8) * mm, "end": v(-9.28, 0.57) * mm});
            skArc(sketch, "E175.0.57", {"start": v(-9.28, 0.57) * mm, "mid": v(-9.3, 0) * mm, "end": v(-9.28, -0.57) * mm});
            skLineSegment(sketch, "E175.0.58", {"start": v(-9.28, -0.57) * mm, "end": v(-9.47, -0.8) * mm});
            skArc(sketch, "E175.0.59", {"start": v(-9.47, -0.8) * mm, "mid": v(-9.45, -1) * mm, "end": v(-9.42, -1.2) * mm});
            skLineSegment(sketch, "E175.0.60", {"start": v(-9.42, -1.2) * mm, "end": v(-9.2, -1.38) * mm});
            skArc(sketch, "E175.0.61", {"start": v(-9.2, -1.38) * mm, "mid": v(-9.1, -1.93) * mm, "end": v(-8.96, -2.48) * mm});
            skLineSegment(sketch, "E175.0.62", {"start": v(-8.96, -2.48) * mm, "end": v(-9.1, -2.74) * mm});
            skArc(sketch, "E175.0.63", {"start": v(-9.1, -2.74) * mm, "mid": v(-9.04, -2.94) * mm, "end": v(-8.97, -3.13) * mm});
            skLineSegment(sketch, "E175.0.64", {"start": v(-8.97, -3.13) * mm, "end": v(-8.71, -3.26) * mm});
            skArc(sketch, "E175.0.65", {"start": v(-8.71, -3.26) * mm, "mid": v(-8.5, -3.78) * mm, "end": v(-8.25, -4.3) * mm});
            skLineSegment(sketch, "E175.0.66", {"start": v(-8.25, -4.3) * mm, "end": v(-8.33, -4.58) * mm});
            skArc(sketch, "E175.0.67", {"start": v(-8.33, -4.58) * mm, "mid": v(-8.23, -4.75) * mm, "end": v(-8.13, -4.92) * mm});
            skLineSegment(sketch, "E175.0.68", {"start": v(-8.13, -4.92) * mm, "end": v(-7.84, -5) * mm});
            skArc(sketch, "E175.0.69", {"start": v(-7.84, -5) * mm, "mid": v(-7.52, -5.47) * mm, "end": v(-7.18, -5.91) * mm});
            skLineSegment(sketch, "E175.0.70", {"start": v(-7.18, -5.91) * mm, "end": v(-7.2, -6.2) * mm});
            skArc(sketch, "E175.0.71", {"start": v(-7.2, -6.2) * mm, "mid": v(-7.06, -6.36) * mm, "end": v(-6.92, -6.5) * mm});
            skLineSegment(sketch, "E175.0.72", {"start": v(-6.92, -6.5) * mm, "end": v(-6.63, -6.52) * mm});
            skArc(sketch, "E175.0.73", {"start": v(-6.63, -6.52) * mm, "mid": v(-6.22, -6.91) * mm, "end": v(-5.8, -7.28) * mm});
            skLineSegment(sketch, "E175.0.74", {"start": v(-5.8, -7.28) * mm, "end": v(-5.74, -7.57) * mm});
            skArc(sketch, "E175.0.75", {"start": v(-5.74, -7.57) * mm, "mid": v(-5.58, -7.69) * mm, "end": v(-5.42, -7.8) * mm});
            skLineSegment(sketch, "E175.0.76", {"start": v(-5.42, -7.8) * mm, "end": v(-5.13, -7.76) * mm});
            skArc(sketch, "E175.0.77", {"start": v(-5.13, -7.76) * mm, "mid": v(-4.65, -8.05) * mm, "end": v(-4.15, -8.32) * mm});
            skLineSegment(sketch, "E175.0.78", {"start": v(-4.15, -8.32) * mm, "end": v(-4.05, -8.6) * mm});
            skArc(sketch, "E175.0.79", {"start": v(-4.05, -8.6) * mm, "mid": v(-3.86, -8.68) * mm, "end": v(-3.68, -8.76) * mm});
            skLineSegment(sketch, "E175.0.80", {"start": v(-3.68, -8.76) * mm, "end": v(-3.4, -8.65) * mm});
            skArc(sketch, "E175.0.81", {"start": v(-3.4, -8.65) * mm, "mid": v(-2.87, -8.84) * mm, "end": v(-2.33, -9) * mm});
            skLineSegment(sketch, "E175.0.82", {"start": v(-2.33, -9) * mm, "end": v(-2.17, -9.25) * mm});
            skArc(sketch, "E175.0.83", {"start": v(-2.17, -9.25) * mm, "mid": v(-1.98, -9.3) * mm, "end": v(-1.78, -9.33) * mm});
            skLineSegment(sketch, "E175.0.84", {"start": v(-1.78, -9.33) * mm, "end": v(-1.53, -9.17) * mm});
            skArc(sketch, "E175.0.85", {"start": v(-1.53, -9.17) * mm, "mid": v(-0.97, -9.25) * mm, "end": v(-0.4, -9.3) * mm});
            skLineSegment(sketch, "E175.0.86", {"start": v(-0.4, -9.3) * mm, "end": v(-0.2, -9.5) * mm});
            skArc(sketch, "E175.0.87", {"start": v(-0.2, -9.5) * mm, "mid": v(0, -9.5) * mm, "end": v(0.2, -9.5) * mm});
            skLineSegment(sketch, "E175.0.88", {"start": v(0.2, -9.5) * mm, "end": v(0.4, -9.3) * mm});
            skArc(sketch, "E175.0.89", {"start": v(0.4, -9.3) * mm, "mid": v(0.97, -9.25) * mm, "end": v(1.53, -9.17) * mm});
            skLineSegment(sketch, "E175.0.90", {"start": v(1.53, -9.17) * mm, "end": v(1.78, -9.33) * mm});
            skArc(sketch, "E175.0.91", {"start": v(1.78, -9.33) * mm, "mid": v(1.98, -9.3) * mm, "end": v(2.17, -9.25) * mm});
            skLineSegment(sketch, "E175.0.92", {"start": v(2.17, -9.25) * mm, "end": v(2.33, -9) * mm});
            skArc(sketch, "E175.0.93", {"start": v(2.33, -9) * mm, "mid": v(2.87, -8.84) * mm, "end": v(3.4, -8.65) * mm});
            skLineSegment(sketch, "E175.0.94", {"start": v(3.4, -8.65) * mm, "end": v(3.68, -8.76) * mm});
            skArc(sketch, "E175.0.95", {"start": v(3.68, -8.76) * mm, "mid": v(3.86, -8.68) * mm, "end": v(4.05, -8.6) * mm});
            skLineSegment(sketch, "E175.0.96", {"start": v(4.05, -8.6) * mm, "end": v(4.15, -8.32) * mm});
            skArc(sketch, "E175.0.97", {"start": v(4.15, -8.32) * mm, "mid": v(4.65, -8.05) * mm, "end": v(5.13, -7.76) * mm});
            skLineSegment(sketch, "E175.0.98", {"start": v(5.13, -7.76) * mm, "end": v(5.42, -7.8) * mm});
            skArc(sketch, "E175.0.99", {"start": v(5.42, -7.8) * mm, "mid": v(5.58, -7.69) * mm, "end": v(5.74, -7.57) * mm});
            skLineSegment(sketch, "E175.0.100", {"start": v(5.74, -7.57) * mm, "end": v(5.8, -7.28) * mm});
            skArc(sketch, "E175.0.101", {"start": v(5.8, -7.28) * mm, "mid": v(6.22, -6.91) * mm, "end": v(6.63, -6.52) * mm});
            skLineSegment(sketch, "E175.0.102", {"start": v(6.63, -6.52) * mm, "end": v(6.92, -6.5) * mm});
            skArc(sketch, "E175.0.103", {"start": v(6.92, -6.5) * mm, "mid": v(7.06, -6.36) * mm, "end": v(7.2, -6.2) * mm});
            skLineSegment(sketch, "E175.0.104", {"start": v(7.2, -6.2) * mm, "end": v(7.18, -5.91) * mm});
            skArc(sketch, "E175.0.105", {"start": v(7.18, -5.91) * mm, "mid": v(7.52, -5.47) * mm, "end": v(7.84, -5) * mm});
            skLineSegment(sketch, "E175.0.106", {"start": v(7.84, -5) * mm, "end": v(8.13, -4.92) * mm});
            skArc(sketch, "E175.0.107", {"start": v(8.13, -4.92) * mm, "mid": v(8.23, -4.75) * mm, "end": v(8.33, -4.58) * mm});
            skLineSegment(sketch, "E175.0.108", {"start": v(8.33, -4.58) * mm, "end": v(8.25, -4.3) * mm});
            skArc(sketch, "E175.0.109", {"start": v(8.25, -4.3) * mm, "mid": v(8.5, -3.78) * mm, "end": v(8.71, -3.26) * mm});
            skLineSegment(sketch, "E175.0.110", {"start": v(8.71, -3.26) * mm, "end": v(8.97, -3.13) * mm});
            skArc(sketch, "E175.0.111", {"start": v(8.97, -3.13) * mm, "mid": v(9.04, -2.94) * mm, "end": v(9.1, -2.74) * mm});
            skLineSegment(sketch, "E175.0.112", {"start": v(9.1, -2.74) * mm, "end": v(8.96, -2.48) * mm});
            skArc(sketch, "E175.0.113", {"start": v(8.96, -2.48) * mm, "mid": v(9.1, -1.93) * mm, "end": v(9.2, -1.38) * mm});
            skLineSegment(sketch, "E175.0.114", {"start": v(9.2, -1.38) * mm, "end": v(9.42, -1.2) * mm});
            skArc(sketch, "E175.0.115", {"start": v(9.42, -1.2) * mm, "mid": v(9.45, -1) * mm, "end": v(9.47, -0.8) * mm});
            skLineSegment(sketch, "E175.0.116", {"start": v(9.47, -0.8) * mm, "end": v(9.28, -0.57) * mm});
            skArc(sketch, "E175.0.117", {"start": v(9.28, -0.57) * mm, "mid": v(9.3, 0) * mm, "end": v(9.28, 0.57) * mm});
            skLineSegment(sketch, "E175.0.118", {"start": v(9.28, 0.57) * mm, "end": v(9.47, 0.8) * mm});
            skArc(sketch, "E175.0.119", {"start": v(9.47, 0.8) * mm, "mid": v(9.45, 1) * mm, "end": v(9.42, 1.2) * mm});
            skSolve(sketch);
        }
        {
            var Q0;
            Q0=makeQuery(id+"F5.imprint","IMPRINT",FACE,{"disambiguationData":[TD([[makeQuery(id+"F5.imprint","IMPRINT",EDGE,{"derivedFrom":sQuery(id+"F5.wireOp",EDGE,"E175.0.0")}),-1.0]])]});
            extrude(context, id + "F6", {"entities" : qUnion([Q0]), "operationType" : NewBodyOperationType.ADD, "depth" : (getVariable(context, 'Bore_Depth_F')) * mm});
        }
        {
            var Q0;
            Q0=makeQuery(id+"F4.opExtrude","CAP_FACE",FACE,{"disambiguationData":[OSD([sQuery(id+"F3.wireOp",EDGE,"E0"),sQuery(id+"F3.wireOp",EDGE,"E1"),sQuery(id+"F3.wireOp",EDGE,"E2"),sQuery(id+"F3.wireOp",EDGE,"E3"),sQuery(id+"F3.wireOp",EDGE,"E4"),sQuery(id+"F3.wireOp",EDGE,"E5"),sQuery(id+"F3.wireOp",EDGE,"E6"),sQuery(id+"F3.wireOp",EDGE,"E7"),sQuery(id+"F3.wireOp",EDGE,"E8"),sQuery(id+"F3.wireOp",EDGE,"E9"),sQuery(id+"F3.wireOp",EDGE,"E10"),sQuery(id+"F3.wireOp",EDGE,"E11"),sQuery(id+"F3.wireOp",EDGE,"E12"),sQuery(id+"F3.wireOp",EDGE,"E13"),sQuery(id+"F3.wireOp",EDGE,"E14"),sQuery(id+"F3.wireOp",EDGE,"E15"),sQuery(id+"F3.wireOp",EDGE,"E16"),sQuery(id+"F3.wireOp",EDGE,"E17"),sQuery(id+"F3.wireOp",EDGE,"E18"),sQuery(id+"F3.wireOp",EDGE,"E19"),sQuery(id+"F3.wireOp",EDGE,"E20"),sQuery(id+"F3.wireOp",EDGE,"E21"),sQuery(id+"F3.wireOp",EDGE,"E22"),sQuery(id+"F3.wireOp",EDGE,"E23"),sQuery(id+"F3.wireOp",EDGE,"E24"),sQuery(id+"F3.wireOp",EDGE,"E25"),sQuery(id+"F3.wireOp",EDGE,"E26"),sQuery(id+"F3.wireOp",EDGE,"E27"),sQuery(id+"F3.wireOp",EDGE,"E28"),sQuery(id+"F3.wireOp",EDGE,"E29"),sQuery(id+"F3.wireOp",EDGE,"E30"),sQuery(id+"F3.wireOp",EDGE,"E31"),sQuery(id+"F3.wireOp",EDGE,"E32"),sQuery(id+"F3.wireOp",EDGE,"E33"),sQuery(id+"F3.wireOp",EDGE,"E34"),sQuery(id+"F3.wireOp",EDGE,"E35"),sQuery(id+"F3.wireOp",EDGE,"E36"),sQuery(id+"F3.wireOp",EDGE,"E37"),sQuery(id+"F3.wireOp",EDGE,"E38"),sQuery(id+"F3.wireOp",EDGE,"E39"),sQuery(id+"F3.wireOp",EDGE,"E40"),sQuery(id+"F3.wireOp",EDGE,"E41"),sQuery(id+"F3.wireOp",EDGE,"E42"),sQuery(id+"F3.wireOp",EDGE,"E43"),sQuery(id+"F3.wireOp",EDGE,"E44"),sQuery(id+"F3.wireOp",EDGE,"E45"),sQuery(id+"F3.wireOp",EDGE,"E46"),sQuery(id+"F3.wireOp",EDGE,"E47"),sQuery(id+"F3.wireOp",EDGE,"E48"),sQuery(id+"F3.wireOp",EDGE,"E49"),sQuery(id+"F3.wireOp",EDGE,"E50"),sQuery(id+"F3.wireOp",EDGE,"E51"),sQuery(id+"F3.wireOp",EDGE,"E52"),sQuery(id+"F3.wireOp",EDGE,"E53"),sQuery(id+"F3.wireOp",EDGE,"E54"),sQuery(id+"F3.wireOp",EDGE,"E55"),sQuery(id+"F3.wireOp",EDGE,"E56"),sQuery(id+"F3.wireOp",EDGE,"E57"),sQuery(id+"F3.wireOp",EDGE,"E58"),sQuery(id+"F3.wireOp",EDGE,"E59"),sQuery(id+"F3.wireOp",EDGE,"E60"),sQuery(id+"F3.wireOp",EDGE,"E61"),sQuery(id+"F3.wireOp",EDGE,"E62"),sQuery(id+"F3.wireOp",EDGE,"E63"),sQuery(id+"F3.wireOp",EDGE,"E64"),sQuery(id+"F3.wireOp",EDGE,"E65"),sQuery(id+"F3.wireOp",EDGE,"E66"),sQuery(id+"F3.wireOp",EDGE,"E67"),sQuery(id+"F3.wireOp",EDGE,"E68"),sQuery(id+"F3.wireOp",EDGE,"E69"),sQuery(id+"F3.wireOp",EDGE,"E70"),sQuery(id+"F3.wireOp",EDGE,"E71"),sQuery(id+"F3.wireOp",EDGE,"E72"),sQuery(id+"F3.wireOp",EDGE,"E73"),sQuery(id+"F3.wireOp",EDGE,"E74"),sQuery(id+"F3.wireOp",EDGE,"E75"),sQuery(id+"F3.wireOp",EDGE,"E76"),sQuery(id+"F3.wireOp",EDGE,"E77"),sQuery(id+"F3.wireOp",EDGE,"E78"),sQuery(id+"F3.wireOp",EDGE,"E79"),sQuery(id+"F3.wireOp",EDGE,"E80"),sQuery(id+"F3.wireOp",EDGE,"E81"),sQuery(id+"F3.wireOp",EDGE,"E82"),sQuery(id+"F3.wireOp",EDGE,"E83"),sQuery(id+"F3.wireOp",EDGE,"E84"),sQuery(id+"F3.wireOp",EDGE,"E85"),sQuery(id+"F3.wireOp",EDGE,"E86"),sQuery(id+"F3.wireOp",EDGE,"E87"),sQuery(id+"F3.wireOp",EDGE,"E88"),sQuery(id+"F3.wireOp",EDGE,"E89"),sQuery(id+"F3.wireOp",EDGE,"E90"),sQuery(id+"F3.wireOp",EDGE,"E91"),sQuery(id+"F3.wireOp",EDGE,"E92"),sQuery(id+"F3.wireOp",EDGE,"E93"),sQuery(id+"F3.wireOp",EDGE,"E94"),sQuery(id+"F3.wireOp",EDGE,"E95"),sQuery(id+"F3.wireOp",EDGE,"E96"),sQuery(id+"F3.wireOp",EDGE,"E97"),sQuery(id+"F3.wireOp",EDGE,"E98"),sQuery(id+"F3.wireOp",EDGE,"E99"),sQuery(id+"F3.wireOp",EDGE,"E100"),sQuery(id+"F3.wireOp",EDGE,"E101"),sQuery(id+"F3.wireOp",EDGE,"E102"),sQuery(id+"F3.wireOp",EDGE,"E103"),sQuery(id+"F3.wireOp",EDGE,"E104"),sQuery(id+"F3.wireOp",EDGE,"E105"),sQuery(id+"F3.wireOp",EDGE,"E106"),sQuery(id+"F3.wireOp",EDGE,"E107"),sQuery(id+"F3.wireOp",EDGE,"E108"),sQuery(id+"F3.wireOp",EDGE,"E109"),sQuery(id+"F3.wireOp",EDGE,"E110"),sQuery(id+"F3.wireOp",EDGE,"E111"),sQuery(id+"F3.wireOp",EDGE,"E112"),sQuery(id+"F3.wireOp",EDGE,"E113"),sQuery(id+"F3.wireOp",EDGE,"E114"),sQuery(id+"F3.wireOp",EDGE,"E115"),sQuery(id+"F3.wireOp",EDGE,"E116"),sQuery(id+"F3.wireOp",EDGE,"E117"),sQuery(id+"F3.wireOp",EDGE,"E118"),sQuery(id+"F3.wireOp",EDGE,"E119"),sQuery(id+"F3.wireOp",EDGE,"E120"),sQuery(id+"F3.wireOp",EDGE,"E121"),sQuery(id+"F3.wireOp",EDGE,"E122"),sQuery(id+"F3.wireOp",EDGE,"E123"),sQuery(id+"F3.wireOp",EDGE,"E124"),sQuery(id+"F3.wireOp",EDGE,"E125"),sQuery(id+"F3.wireOp",EDGE,"E126"),sQuery(id+"F3.wireOp",EDGE,"E127"),sQuery(id+"F3.wireOp",EDGE,"E128"),sQuery(id+"F3.wireOp",EDGE,"E129"),sQuery(id+"F3.wireOp",EDGE,"E130"),sQuery(id+"F3.wireOp",EDGE,"E131"),sQuery(id+"F3.wireOp",EDGE,"E132"),sQuery(id+"F3.wireOp",EDGE,"E133"),sQuery(id+"F3.wireOp",EDGE,"E134"),sQuery(id+"F3.wireOp",EDGE,"E135"),sQuery(id+"F3.wireOp",EDGE,"E136"),sQuery(id+"F3.wireOp",EDGE,"E137"),sQuery(id+"F3.wireOp",EDGE,"E138"),sQuery(id+"F3.wireOp",EDGE,"E139"),sQuery(id+"F3.wireOp",EDGE,"E140"),sQuery(id+"F3.wireOp",EDGE,"E141"),sQuery(id+"F3.wireOp",EDGE,"E142"),sQuery(id+"F3.wireOp",EDGE,"E143"),sQuery(id+"F3.wireOp",EDGE,"E144"),sQuery(id+"F3.wireOp",EDGE,"E145"),sQuery(id+"F3.wireOp",EDGE,"E146"),sQuery(id+"F3.wireOp",EDGE,"E147"),sQuery(id+"F3.wireOp",EDGE,"E148"),sQuery(id+"F3.wireOp",EDGE,"E149"),sQuery(id+"F3.wireOp",EDGE,"E150"),sQuery(id+"F3.wireOp",EDGE,"E151"),sQuery(id+"F3.wireOp",EDGE,"E152"),sQuery(id+"F3.wireOp",EDGE,"E153"),sQuery(id+"F3.wireOp",EDGE,"E154"),sQuery(id+"F3.wireOp",EDGE,"E155"),sQuery(id+"F3.wireOp",EDGE,"E156"),sQuery(id+"F3.wireOp",EDGE,"E157"),sQuery(id+"F3.wireOp",EDGE,"E158"),sQuery(id+"F3.wireOp",EDGE,"E159"),sQuery(id+"F3.wireOp",EDGE,"E160"),sQuery(id+"F3.wireOp",EDGE,"E161"),sQuery(id+"F3.wireOp",EDGE,"E162"),sQuery(id+"F3.wireOp",EDGE,"E163"),sQuery(id+"F3.wireOp",EDGE,"E164"),sQuery(id+"F3.wireOp",EDGE,"E165"),sQuery(id+"F3.wireOp",EDGE,"E166"),sQuery(id+"F3.wireOp",EDGE,"E167"),sQuery(id+"F3.wireOp",EDGE,"E168"),sQuery(id+"F3.wireOp",EDGE,"E169"),sQuery(id+"F3.wireOp",EDGE,"E170"),sQuery(id+"F3.wireOp",EDGE,"E171"),sQuery(id+"F3.wireOp",EDGE,"E172"),sQuery(id+"F3.wireOp",EDGE,"E173")])],"isStart":true});
            var sketch = newSketch(context, id + "F7", { "sketchPlane" : qUnion([Q0])});
            skCircle(sketch, "E176", {"center": v(0, 0) * mm, "radius": 8 * mm});
            skLineSegment(sketch, "E177.0.0", {"start": v(-9.2, 1.38) * mm, "end": v(-9.42, 1.2) * mm});
            skArc(sketch, "E177.0.1", {"start": v(-9.42, 1.2) * mm, "mid": v(-9.45, 1) * mm, "end": v(-9.47, 0.8) * mm});
            skLineSegment(sketch, "E177.0.2", {"start": v(-9.47, 0.8) * mm, "end": v(-9.28, 0.57) * mm});
            skArc(sketch, "E177.0.3", {"start": v(-9.28, 0.57) * mm, "mid": v(-9.3, 0) * mm, "end": v(-9.28, -0.57) * mm});
            skLineSegment(sketch, "E177.0.4", {"start": v(-9.28, -0.57) * mm, "end": v(-9.47, -0.8) * mm});
            skArc(sketch, "E177.0.5", {"start": v(-9.47, -0.8) * mm, "mid": v(-9.45, -1) * mm, "end": v(-9.42, -1.2) * mm});
            skLineSegment(sketch, "E177.0.6", {"start": v(-9.42, -1.2) * mm, "end": v(-9.2, -1.38) * mm});
            skArc(sketch, "E177.0.7", {"start": v(-9.2, -1.38) * mm, "mid": v(-9.1, -1.93) * mm, "end": v(-8.96, -2.48) * mm});
            skLineSegment(sketch, "E177.0.8", {"start": v(-8.96, -2.48) * mm, "end": v(-9.1, -2.74) * mm});
            skArc(sketch, "E177.0.9", {"start": v(-9.1, -2.74) * mm, "mid": v(-9.04, -2.94) * mm, "end": v(-8.97, -3.13) * mm});
            skLineSegment(sketch, "E177.0.10", {"start": v(-8.97, -3.13) * mm, "end": v(-8.71, -3.26) * mm});
            skArc(sketch, "E177.0.11", {"start": v(-8.71, -3.26) * mm, "mid": v(-8.5, -3.78) * mm, "end": v(-8.25, -4.3) * mm});
            skLineSegment(sketch, "E177.0.12", {"start": v(-8.25, -4.3) * mm, "end": v(-8.33, -4.58) * mm});
            skArc(sketch, "E177.0.13", {"start": v(-8.33, -4.58) * mm, "mid": v(-8.23, -4.75) * mm, "end": v(-8.13, -4.92) * mm});
            skLineSegment(sketch, "E177.0.14", {"start": v(-8.13, -4.92) * mm, "end": v(-7.84, -5) * mm});
            skArc(sketch, "E177.0.15", {"start": v(-7.84, -5) * mm, "mid": v(-7.52, -5.47) * mm, "end": v(-7.18, -5.91) * mm});
            skLineSegment(sketch, "E177.0.16", {"start": v(-7.18, -5.91) * mm, "end": v(-7.2, -6.2) * mm});
            skArc(sketch, "E177.0.17", {"start": v(-7.2, -6.2) * mm, "mid": v(-7.06, -6.36) * mm, "end": v(-6.92, -6.5) * mm});
            skLineSegment(sketch, "E177.0.18", {"start": v(-6.92, -6.5) * mm, "end": v(-6.63, -6.52) * mm});
            skArc(sketch, "E177.0.19", {"start": v(-6.63, -6.52) * mm, "mid": v(-6.22, -6.91) * mm, "end": v(-5.8, -7.28) * mm});
            skLineSegment(sketch, "E177.0.20", {"start": v(-5.8, -7.28) * mm, "end": v(-5.74, -7.57) * mm});
            skArc(sketch, "E177.0.21", {"start": v(-5.74, -7.57) * mm, "mid": v(-5.58, -7.69) * mm, "end": v(-5.42, -7.8) * mm});
            skLineSegment(sketch, "E177.0.22", {"start": v(-5.42, -7.8) * mm, "end": v(-5.13, -7.76) * mm});
            skArc(sketch, "E177.0.23", {"start": v(-5.13, -7.76) * mm, "mid": v(-4.65, -8.05) * mm, "end": v(-4.15, -8.32) * mm});
            skLineSegment(sketch, "E177.0.24", {"start": v(-4.15, -8.32) * mm, "end": v(-4.05, -8.6) * mm});
            skArc(sketch, "E177.0.25", {"start": v(-4.05, -8.6) * mm, "mid": v(-3.86, -8.68) * mm, "end": v(-3.68, -8.76) * mm});
            skLineSegment(sketch, "E177.0.26", {"start": v(-3.68, -8.76) * mm, "end": v(-3.4, -8.65) * mm});
            skArc(sketch, "E177.0.27", {"start": v(-3.4, -8.65) * mm, "mid": v(-2.87, -8.84) * mm, "end": v(-2.33, -9) * mm});
            skLineSegment(sketch, "E177.0.28", {"start": v(-2.33, -9) * mm, "end": v(-2.17, -9.25) * mm});
            skArc(sketch, "E177.0.29", {"start": v(-2.17, -9.25) * mm, "mid": v(-1.98, -9.3) * mm, "end": v(-1.78, -9.33) * mm});
            skLineSegment(sketch, "E177.0.30", {"start": v(-1.78, -9.33) * mm, "end": v(-1.53, -9.17) * mm});
            skArc(sketch, "E177.0.31", {"start": v(-1.53, -9.17) * mm, "mid": v(-0.97, -9.25) * mm, "end": v(-0.4, -9.3) * mm});
            skLineSegment(sketch, "E177.0.32", {"start": v(-0.4, -9.3) * mm, "end": v(-0.2, -9.5) * mm});
            skArc(sketch, "E177.0.33", {"start": v(-0.2, -9.5) * mm, "mid": v(0, -9.5) * mm, "end": v(0.2, -9.5) * mm});
            skLineSegment(sketch, "E177.0.34", {"start": v(0.2, -9.5) * mm, "end": v(0.4, -9.3) * mm});
            skArc(sketch, "E177.0.35", {"start": v(0.4, -9.3) * mm, "mid": v(0.97, -9.25) * mm, "end": v(1.53, -9.17) * mm});
            skLineSegment(sketch, "E177.0.36", {"start": v(1.53, -9.17) * mm, "end": v(1.78, -9.33) * mm});
            skArc(sketch, "E177.0.37", {"start": v(1.78, -9.33) * mm, "mid": v(1.98, -9.3) * mm, "end": v(2.17, -9.25) * mm});
            skLineSegment(sketch, "E177.0.38", {"start": v(2.17, -9.25) * mm, "end": v(2.33, -9) * mm});
            skArc(sketch, "E177.0.39", {"start": v(2.33, -9) * mm, "mid": v(2.87, -8.84) * mm, "end": v(3.4, -8.65) * mm});
            skLineSegment(sketch, "E177.0.40", {"start": v(3.4, -8.65) * mm, "end": v(3.68, -8.76) * mm});
            skArc(sketch, "E177.0.41", {"start": v(3.68, -8.76) * mm, "mid": v(3.86, -8.68) * mm, "end": v(4.05, -8.6) * mm});
            skLineSegment(sketch, "E177.0.42", {"start": v(4.05, -8.6) * mm, "end": v(4.15, -8.32) * mm});
            skArc(sketch, "E177.0.43", {"start": v(4.15, -8.32) * mm, "mid": v(4.65, -8.05) * mm, "end": v(5.13, -7.76) * mm});
            skLineSegment(sketch, "E177.0.44", {"start": v(5.13, -7.76) * mm, "end": v(5.42, -7.8) * mm});
            skArc(sketch, "E177.0.45", {"start": v(5.42, -7.8) * mm, "mid": v(5.58, -7.69) * mm, "end": v(5.74, -7.57) * mm});
            skLineSegment(sketch, "E177.0.46", {"start": v(5.74, -7.57) * mm, "end": v(5.8, -7.28) * mm});
            skArc(sketch, "E177.0.47", {"start": v(5.8, -7.28) * mm, "mid": v(6.22, -6.91) * mm, "end": v(6.63, -6.52) * mm});
            skLineSegment(sketch, "E177.0.48", {"start": v(6.63, -6.52) * mm, "end": v(6.92, -6.5) * mm});
            skArc(sketch, "E177.0.49", {"start": v(6.92, -6.5) * mm, "mid": v(7.06, -6.36) * mm, "end": v(7.2, -6.2) * mm});
            skLineSegment(sketch, "E177.0.50", {"start": v(7.2, -6.2) * mm, "end": v(7.18, -5.91) * mm});
            skArc(sketch, "E177.0.51", {"start": v(7.18, -5.91) * mm, "mid": v(7.52, -5.47) * mm, "end": v(7.84, -5) * mm});
            skLineSegment(sketch, "E177.0.52", {"start": v(7.84, -5) * mm, "end": v(8.13, -4.92) * mm});
            skArc(sketch, "E177.0.53", {"start": v(8.13, -4.92) * mm, "mid": v(8.23, -4.75) * mm, "end": v(8.33, -4.58) * mm});
            skLineSegment(sketch, "E177.0.54", {"start": v(8.33, -4.58) * mm, "end": v(8.25, -4.3) * mm});
            skArc(sketch, "E177.0.55", {"start": v(8.25, -4.3) * mm, "mid": v(8.5, -3.78) * mm, "end": v(8.71, -3.26) * mm});
            skLineSegment(sketch, "E177.0.56", {"start": v(8.71, -3.26) * mm, "end": v(8.97, -3.13) * mm});
            skArc(sketch, "E177.0.57", {"start": v(8.97, -3.13) * mm, "mid": v(9.04, -2.94) * mm, "end": v(9.1, -2.74) * mm});
            skLineSegment(sketch, "E177.0.58", {"start": v(9.1, -2.74) * mm, "end": v(8.96, -2.48) * mm});
            skArc(sketch, "E177.0.59", {"start": v(8.96, -2.48) * mm, "mid": v(9.1, -1.93) * mm, "end": v(9.2, -1.38) * mm});
            skLineSegment(sketch, "E177.0.60", {"start": v(9.2, -1.38) * mm, "end": v(9.42, -1.2) * mm});
            skArc(sketch, "E177.0.61", {"start": v(9.42, -1.2) * mm, "mid": v(9.45, -1) * mm, "end": v(9.47, -0.8) * mm});
            skLineSegment(sketch, "E177.0.62", {"start": v(9.47, -0.8) * mm, "end": v(9.28, -0.57) * mm});
            skArc(sketch, "E177.0.63", {"start": v(9.28, -0.57) * mm, "mid": v(9.3, 0) * mm, "end": v(9.28, 0.57) * mm});
            skLineSegment(sketch, "E177.0.64", {"start": v(9.28, 0.57) * mm, "end": v(9.47, 0.8) * mm});
            skArc(sketch, "E177.0.65", {"start": v(9.47, 0.8) * mm, "mid": v(9.45, 1) * mm, "end": v(9.42, 1.2) * mm});
            skLineSegment(sketch, "E177.0.66", {"start": v(9.42, 1.2) * mm, "end": v(9.2, 1.38) * mm});
            skArc(sketch, "E177.0.67", {"start": v(9.2, 1.38) * mm, "mid": v(9.1, 1.93) * mm, "end": v(8.96, 2.48) * mm});
            skLineSegment(sketch, "E177.0.68", {"start": v(8.96, 2.48) * mm, "end": v(9.1, 2.74) * mm});
            skArc(sketch, "E177.0.69", {"start": v(9.1, 2.74) * mm, "mid": v(9.04, 2.94) * mm, "end": v(8.97, 3.13) * mm});
            skLineSegment(sketch, "E177.0.70", {"start": v(8.97, 3.13) * mm, "end": v(8.71, 3.26) * mm});
            skArc(sketch, "E177.0.71", {"start": v(8.71, 3.26) * mm, "mid": v(8.5, 3.78) * mm, "end": v(8.25, 4.3) * mm});
            skLineSegment(sketch, "E177.0.72", {"start": v(8.25, 4.3) * mm, "end": v(8.33, 4.58) * mm});
            skArc(sketch, "E177.0.73", {"start": v(8.33, 4.58) * mm, "mid": v(8.23, 4.75) * mm, "end": v(8.13, 4.92) * mm});
            skLineSegment(sketch, "E177.0.74", {"start": v(8.13, 4.92) * mm, "end": v(7.84, 5) * mm});
            skArc(sketch, "E177.0.75", {"start": v(7.84, 5) * mm, "mid": v(7.52, 5.47) * mm, "end": v(7.18, 5.91) * mm});
            skLineSegment(sketch, "E177.0.76", {"start": v(7.18, 5.91) * mm, "end": v(7.2, 6.2) * mm});
            skArc(sketch, "E177.0.77", {"start": v(7.2, 6.2) * mm, "mid": v(7.06, 6.36) * mm, "end": v(6.92, 6.5) * mm});
            skLineSegment(sketch, "E177.0.78", {"start": v(6.92, 6.5) * mm, "end": v(6.63, 6.52) * mm});
            skArc(sketch, "E177.0.79", {"start": v(6.63, 6.52) * mm, "mid": v(6.22, 6.91) * mm, "end": v(5.8, 7.28) * mm});
            skLineSegment(sketch, "E177.0.80", {"start": v(5.8, 7.28) * mm, "end": v(5.74, 7.57) * mm});
            skArc(sketch, "E177.0.81", {"start": v(5.74, 7.57) * mm, "mid": v(5.58, 7.69) * mm, "end": v(5.42, 7.8) * mm});
            skLineSegment(sketch, "E177.0.82", {"start": v(5.42, 7.8) * mm, "end": v(5.13, 7.76) * mm});
            skArc(sketch, "E177.0.83", {"start": v(5.13, 7.76) * mm, "mid": v(4.65, 8.05) * mm, "end": v(4.15, 8.32) * mm});
            skLineSegment(sketch, "E177.0.84", {"start": v(4.15, 8.32) * mm, "end": v(4.05, 8.6) * mm});
            skArc(sketch, "E177.0.85", {"start": v(4.05, 8.6) * mm, "mid": v(3.86, 8.68) * mm, "end": v(3.68, 8.76) * mm});
            skLineSegment(sketch, "E177.0.86", {"start": v(3.68, 8.76) * mm, "end": v(3.4, 8.65) * mm});
            skArc(sketch, "E177.0.87", {"start": v(3.4, 8.65) * mm, "mid": v(2.87, 8.84) * mm, "end": v(2.33, 9) * mm});
            skLineSegment(sketch, "E177.0.88", {"start": v(2.33, 9) * mm, "end": v(2.17, 9.25) * mm});
            skArc(sketch, "E177.0.89", {"start": v(2.17, 9.25) * mm, "mid": v(1.98, 9.3) * mm, "end": v(1.78, 9.33) * mm});
            skLineSegment(sketch, "E177.0.90", {"start": v(1.78, 9.33) * mm, "end": v(1.53, 9.17) * mm});
            skArc(sketch, "E177.0.91", {"start": v(1.53, 9.17) * mm, "mid": v(0.97, 9.25) * mm, "end": v(0.4, 9.3) * mm});
            skLineSegment(sketch, "E177.0.92", {"start": v(0.4, 9.3) * mm, "end": v(0.2, 9.5) * mm});
            skArc(sketch, "E177.0.93", {"start": v(0.2, 9.5) * mm, "mid": v(0, 9.5) * mm, "end": v(-0.2, 9.5) * mm});
            skLineSegment(sketch, "E177.0.94", {"start": v(-0.2, 9.5) * mm, "end": v(-0.4, 9.3) * mm});
            skArc(sketch, "E177.0.95", {"start": v(-0.4, 9.3) * mm, "mid": v(-0.97, 9.25) * mm, "end": v(-1.53, 9.17) * mm});
            skLineSegment(sketch, "E177.0.96", {"start": v(-1.53, 9.17) * mm, "end": v(-1.78, 9.33) * mm});
            skArc(sketch, "E177.0.97", {"start": v(-1.78, 9.33) * mm, "mid": v(-1.98, 9.3) * mm, "end": v(-2.17, 9.25) * mm});
            skLineSegment(sketch, "E177.0.98", {"start": v(-2.17, 9.25) * mm, "end": v(-2.33, 9) * mm});
            skArc(sketch, "E177.0.99", {"start": v(-2.33, 9) * mm, "mid": v(-2.87, 8.84) * mm, "end": v(-3.4, 8.65) * mm});
            skLineSegment(sketch, "E177.0.100", {"start": v(-3.4, 8.65) * mm, "end": v(-3.68, 8.76) * mm});
            skArc(sketch, "E177.0.101", {"start": v(-3.68, 8.76) * mm, "mid": v(-3.86, 8.68) * mm, "end": v(-4.05, 8.6) * mm});
            skLineSegment(sketch, "E177.0.102", {"start": v(-4.05, 8.6) * mm, "end": v(-4.15, 8.32) * mm});
            skArc(sketch, "E177.0.103", {"start": v(-4.15, 8.32) * mm, "mid": v(-4.65, 8.05) * mm, "end": v(-5.13, 7.76) * mm});
            skLineSegment(sketch, "E177.0.104", {"start": v(-5.13, 7.76) * mm, "end": v(-5.42, 7.8) * mm});
            skArc(sketch, "E177.0.105", {"start": v(-5.42, 7.8) * mm, "mid": v(-5.58, 7.69) * mm, "end": v(-5.74, 7.57) * mm});
            skLineSegment(sketch, "E177.0.106", {"start": v(-5.74, 7.57) * mm, "end": v(-5.8, 7.28) * mm});
            skArc(sketch, "E177.0.107", {"start": v(-5.8, 7.28) * mm, "mid": v(-6.22, 6.91) * mm, "end": v(-6.63, 6.52) * mm});
            skLineSegment(sketch, "E177.0.108", {"start": v(-6.63, 6.52) * mm, "end": v(-6.92, 6.5) * mm});
            skArc(sketch, "E177.0.109", {"start": v(-6.92, 6.5) * mm, "mid": v(-7.06, 6.36) * mm, "end": v(-7.2, 6.2) * mm});
            skLineSegment(sketch, "E177.0.110", {"start": v(-7.2, 6.2) * mm, "end": v(-7.18, 5.91) * mm});
            skArc(sketch, "E177.0.111", {"start": v(-7.18, 5.91) * mm, "mid": v(-7.52, 5.47) * mm, "end": v(-7.84, 5) * mm});
            skLineSegment(sketch, "E177.0.112", {"start": v(-7.84, 5) * mm, "end": v(-8.13, 4.92) * mm});
            skArc(sketch, "E177.0.113", {"start": v(-8.13, 4.92) * mm, "mid": v(-8.23, 4.75) * mm, "end": v(-8.33, 4.58) * mm});
            skLineSegment(sketch, "E177.0.114", {"start": v(-8.33, 4.58) * mm, "end": v(-8.25, 4.3) * mm});
            skArc(sketch, "E177.0.115", {"start": v(-8.25, 4.3) * mm, "mid": v(-8.5, 3.78) * mm, "end": v(-8.71, 3.26) * mm});
            skLineSegment(sketch, "E177.0.116", {"start": v(-8.71, 3.26) * mm, "end": v(-8.97, 3.13) * mm});
            skArc(sketch, "E177.0.117", {"start": v(-8.97, 3.13) * mm, "mid": v(-9.04, 2.94) * mm, "end": v(-9.1, 2.74) * mm});
            skLineSegment(sketch, "E177.0.118", {"start": v(-9.1, 2.74) * mm, "end": v(-8.96, 2.48) * mm});
            skArc(sketch, "E177.0.119", {"start": v(-8.96, 2.48) * mm, "mid": v(-9.1, 1.93) * mm, "end": v(-9.2, 1.38) * mm});
            skSolve(sketch);
        }
        {
            var Q0;
            Q0=makeQuery(id+"F7.imprint","IMPRINT",FACE,{"disambiguationData":[TD([[makeQuery(id+"F7.imprint","IMPRINT",EDGE,{"derivedFrom":sQuery(id+"F7.wireOp",EDGE,"E177.0.0")}),1.0]])]});
            extrude(context, id + "F8", {"entities" : qUnion([Q0]), "operationType" : NewBodyOperationType.ADD, "depth" : (getVariable(context, 'Bore_Depth_R')) * mm});
        }
        {
            var Q0;
            Q0=qCreatedBy(makeId("Right.planeOp"),FACE);
            var sketch = newSketch(context, id + "F9", { "sketchPlane" : qUnion([Q0])});
            skCircle(sketch, "E178", {"center": v(-58, 0) * mm, "radius": 3.25 * mm});
            skPoint(sketch, "E179", {"position": v(-56.13, 0) * mm});
            skCircle(sketch, "E180", {"center": v(26, 0) * mm, "radius": 1.25 * mm});
            skCircle(sketch, "E181", {"center": v(-67, 0) * mm, "radius": 1.25 * mm});
            skSolve(sketch);
        }
        {
            var Q0;
            Q0=makeQuery(id+"F6.opExtrude","CAP_FACE",FACE,{"disambiguationData":[OSD([sQuery(id+"F5.wireOp",EDGE,"E174"),sQuery(id+"F5.wireOp",EDGE,"E175.0.0"),sQuery(id+"F5.wireOp",EDGE,"E175.0.1"),sQuery(id+"F5.wireOp",EDGE,"E175.0.2"),sQuery(id+"F5.wireOp",EDGE,"E175.0.3"),sQuery(id+"F5.wireOp",EDGE,"E175.0.4"),sQuery(id+"F5.wireOp",EDGE,"E175.0.5"),sQuery(id+"F5.wireOp",EDGE,"E175.0.6"),sQuery(id+"F5.wireOp",EDGE,"E175.0.7"),sQuery(id+"F5.wireOp",EDGE,"E175.0.8"),sQuery(id+"F5.wireOp",EDGE,"E175.0.9"),sQuery(id+"F5.wireOp",EDGE,"E175.0.10"),sQuery(id+"F5.wireOp",EDGE,"E175.0.11"),sQuery(id+"F5.wireOp",EDGE,"E175.0.12"),sQuery(id+"F5.wireOp",EDGE,"E175.0.13"),sQuery(id+"F5.wireOp",EDGE,"E175.0.14"),sQuery(id+"F5.wireOp",EDGE,"E175.0.15"),sQuery(id+"F5.wireOp",EDGE,"E175.0.16"),sQuery(id+"F5.wireOp",EDGE,"E175.0.17"),sQuery(id+"F5.wireOp",EDGE,"E175.0.18"),sQuery(id+"F5.wireOp",EDGE,"E175.0.19"),sQuery(id+"F5.wireOp",EDGE,"E175.0.20"),sQuery(id+"F5.wireOp",EDGE,"E175.0.21"),sQuery(id+"F5.wireOp",EDGE,"E175.0.22"),sQuery(id+"F5.wireOp",EDGE,"E175.0.23"),sQuery(id+"F5.wireOp",EDGE,"E175.0.24"),sQuery(id+"F5.wireOp",EDGE,"E175.0.25"),sQuery(id+"F5.wireOp",EDGE,"E175.0.26"),sQuery(id+"F5.wireOp",EDGE,"E175.0.27"),sQuery(id+"F5.wireOp",EDGE,"E175.0.28"),sQuery(id+"F5.wireOp",EDGE,"E175.0.29"),sQuery(id+"F5.wireOp",EDGE,"E175.0.30"),sQuery(id+"F5.wireOp",EDGE,"E175.0.31"),sQuery(id+"F5.wireOp",EDGE,"E175.0.32"),sQuery(id+"F5.wireOp",EDGE,"E175.0.33"),sQuery(id+"F5.wireOp",EDGE,"E175.0.34"),sQuery(id+"F5.wireOp",EDGE,"E175.0.35"),sQuery(id+"F5.wireOp",EDGE,"E175.0.36"),sQuery(id+"F5.wireOp",EDGE,"E175.0.37"),sQuery(id+"F5.wireOp",EDGE,"E175.0.38"),sQuery(id+"F5.wireOp",EDGE,"E175.0.39"),sQuery(id+"F5.wireOp",EDGE,"E175.0.40"),sQuery(id+"F5.wireOp",EDGE,"E175.0.41"),sQuery(id+"F5.wireOp",EDGE,"E175.0.42"),sQuery(id+"F5.wireOp",EDGE,"E175.0.43"),sQuery(id+"F5.wireOp",EDGE,"E175.0.44"),sQuery(id+"F5.wireOp",EDGE,"E175.0.45"),sQuery(id+"F5.wireOp",EDGE,"E175.0.46"),sQuery(id+"F5.wireOp",EDGE,"E175.0.47"),sQuery(id+"F5.wireOp",EDGE,"E175.0.48"),sQuery(id+"F5.wireOp",EDGE,"E175.0.49"),sQuery(id+"F5.wireOp",EDGE,"E175.0.50"),sQuery(id+"F5.wireOp",EDGE,"E175.0.51"),sQuery(id+"F5.wireOp",EDGE,"E175.0.52"),sQuery(id+"F5.wireOp",EDGE,"E175.0.53"),sQuery(id+"F5.wireOp",EDGE,"E175.0.54"),sQuery(id+"F5.wireOp",EDGE,"E175.0.55"),sQuery(id+"F5.wireOp",EDGE,"E175.0.56"),sQuery(id+"F5.wireOp",EDGE,"E175.0.57"),sQuery(id+"F5.wireOp",EDGE,"E175.0.58"),sQuery(id+"F5.wireOp",EDGE,"E175.0.59"),sQuery(id+"F5.wireOp",EDGE,"E175.0.60"),sQuery(id+"F5.wireOp",EDGE,"E175.0.61"),sQuery(id+"F5.wireOp",EDGE,"E175.0.62"),sQuery(id+"F5.wireOp",EDGE,"E175.0.63"),sQuery(id+"F5.wireOp",EDGE,"E175.0.64"),sQuery(id+"F5.wireOp",EDGE,"E175.0.65"),sQuery(id+"F5.wireOp",EDGE,"E175.0.66"),sQuery(id+"F5.wireOp",EDGE,"E175.0.67"),sQuery(id+"F5.wireOp",EDGE,"E175.0.68"),sQuery(id+"F5.wireOp",EDGE,"E175.0.69"),sQuery(id+"F5.wireOp",EDGE,"E175.0.70"),sQuery(id+"F5.wireOp",EDGE,"E175.0.71"),sQuery(id+"F5.wireOp",EDGE,"E175.0.72"),sQuery(id+"F5.wireOp",EDGE,"E175.0.73"),sQuery(id+"F5.wireOp",EDGE,"E175.0.74"),sQuery(id+"F5.wireOp",EDGE,"E175.0.75"),sQuery(id+"F5.wireOp",EDGE,"E175.0.76"),sQuery(id+"F5.wireOp",EDGE,"E175.0.77"),sQuery(id+"F5.wireOp",EDGE,"E175.0.78"),sQuery(id+"F5.wireOp",EDGE,"E175.0.79"),sQuery(id+"F5.wireOp",EDGE,"E175.0.80"),sQuery(id+"F5.wireOp",EDGE,"E175.0.81"),sQuery(id+"F5.wireOp",EDGE,"E175.0.82"),sQuery(id+"F5.wireOp",EDGE,"E175.0.83"),sQuery(id+"F5.wireOp",EDGE,"E175.0.84"),sQuery(id+"F5.wireOp",EDGE,"E175.0.85"),sQuery(id+"F5.wireOp",EDGE,"E175.0.86"),sQuery(id+"F5.wireOp",EDGE,"E175.0.87"),sQuery(id+"F5.wireOp",EDGE,"E175.0.88"),sQuery(id+"F5.wireOp",EDGE,"E175.0.89"),sQuery(id+"F5.wireOp",EDGE,"E175.0.90"),sQuery(id+"F5.wireOp",EDGE,"E175.0.91"),sQuery(id+"F5.wireOp",EDGE,"E175.0.92"),sQuery(id+"F5.wireOp",EDGE,"E175.0.93"),sQuery(id+"F5.wireOp",EDGE,"E175.0.94"),sQuery(id+"F5.wireOp",EDGE,"E175.0.95"),sQuery(id+"F5.wireOp",EDGE,"E175.0.96"),sQuery(id+"F5.wireOp",EDGE,"E175.0.97"),sQuery(id+"F5.wireOp",EDGE,"E175.0.98"),sQuery(id+"F5.wireOp",EDGE,"E175.0.99"),sQuery(id+"F5.wireOp",EDGE,"E175.0.100"),sQuery(id+"F5.wireOp",EDGE,"E175.0.101"),sQuery(id+"F5.wireOp",EDGE,"E175.0.102"),sQuery(id+"F5.wireOp",EDGE,"E175.0.103"),sQuery(id+"F5.wireOp",EDGE,"E175.0.104"),sQuery(id+"F5.wireOp",EDGE,"E175.0.105"),sQuery(id+"F5.wireOp",EDGE,"E175.0.106"),sQuery(id+"F5.wireOp",EDGE,"E175.0.107"),sQuery(id+"F5.wireOp",EDGE,"E175.0.108"),sQuery(id+"F5.wireOp",EDGE,"E175.0.109"),sQuery(id+"F5.wireOp",EDGE,"E175.0.110"),sQuery(id+"F5.wireOp",EDGE,"E175.0.111"),sQuery(id+"F5.wireOp",EDGE,"E175.0.112"),sQuery(id+"F5.wireOp",EDGE,"E175.0.113"),sQuery(id+"F5.wireOp",EDGE,"E175.0.114"),sQuery(id+"F5.wireOp",EDGE,"E175.0.115"),sQuery(id+"F5.wireOp",EDGE,"E175.0.116"),sQuery(id+"F5.wireOp",EDGE,"E175.0.117"),sQuery(id+"F5.wireOp",EDGE,"E175.0.118"),sQuery(id+"F5.wireOp",EDGE,"E175.0.119")])],"isStart":false});
            var sketch = newSketch(context, id + "F10", { "sketchPlane" : qUnion([Q0])});
            skCircle(sketch, "E182", {"center": v(0, 0) * mm, "radius": 9.5 * mm});
            skCircle(sketch, "E183", {"center": v(0, 0) * mm, "radius": 8 * mm});
            skSolve(sketch);
        }
        {
            var Q0;
            Q0 = qSketchRegion(id + "F10", true);
            extrude(context, id + "F11", {"entities" : qUnion([Q0]), "oppositeDirection" : true, "depth" : (getVariable(context, 'Main_Length')) * mm});
        }
        {
            var Q0;
            Q0=makeQuery(id+"F9.imprint","IMPRINT",FACE,{"disambiguationData":[TD([[makeQuery(id+"F9.imprint","IMPRINT",EDGE,{"derivedFrom":sQuery(id+"F9.wireOp",EDGE,"E178")}),1.0]])]});
            var Q1;
            Q1=makeQuery(id+"F9.imprint","IMPRINT",FACE,{"disambiguationData":[TD([[makeQuery(id+"F9.imprint","IMPRINT",EDGE,{"derivedFrom":sQuery(id+"F9.wireOp",EDGE,"E181")}),1.0]])]});
            extrude(context, id + "F12", {"entities" : qUnion([Q0, Q1]), "operationType" : NewBodyOperationType.REMOVE, "endBound" : BoundingType.THROUGH_ALL, "oppositeDirection" : true, "depth" : 5 * mm});
        }
        {
            var Q0;
            Q0=makeQuery(id+"F9.imprint","IMPRINT",FACE,{"disambiguationData":[TD([[makeQuery(id+"F9.imprint","IMPRINT",EDGE,{"derivedFrom":sQuery(id+"F9.wireOp",EDGE,"E181")}),1.0]])]});
            var Q1;
            Q1=makeQuery(id+"F9.imprint","IMPRINT",FACE,{"disambiguationData":[TD([[makeQuery(id+"F9.imprint","IMPRINT",EDGE,{"derivedFrom":sQuery(id+"F9.wireOp",EDGE,"E180")}),1.0]])]});
            extrude(context, id + "F13", {"entities" : qUnion([Q0, Q1]), "operationType" : NewBodyOperationType.REMOVE, "endBound" : BoundingType.THROUGH_ALL, "depth" : 25 * mm});
        }
    });
